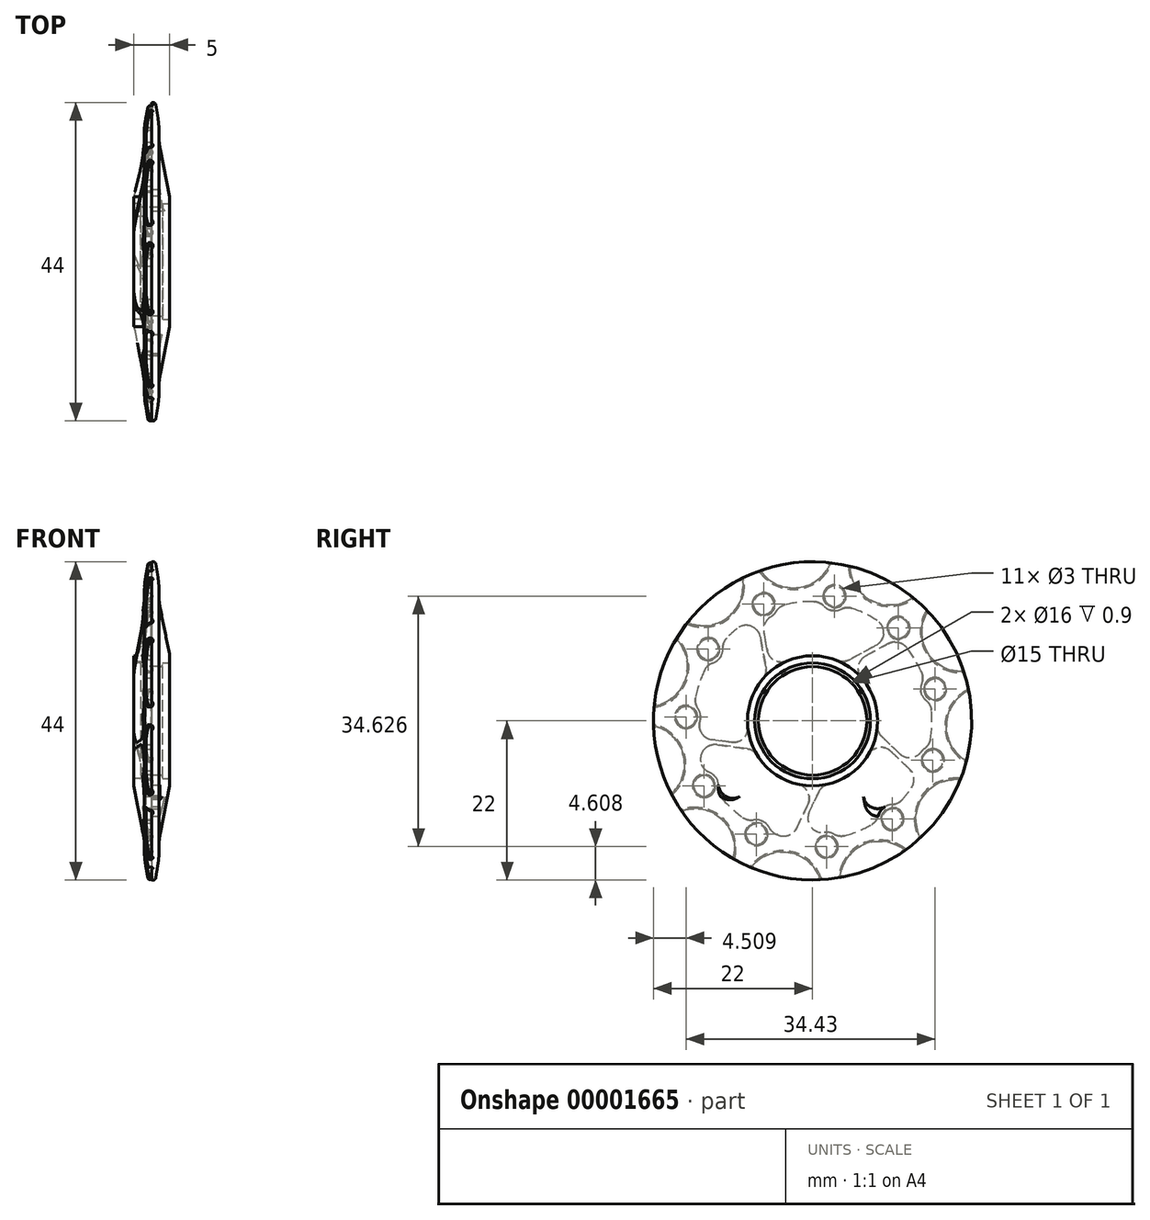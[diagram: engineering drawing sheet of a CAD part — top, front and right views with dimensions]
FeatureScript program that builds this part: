
annotation { "Feature Type Name" : "Feature", "Feature Type Description" : "" }
export const myFeature = defineFeature(function(context is Context, id is Id, definition is map)
    precondition{}
    {
        {
            var Q0;
            Q0=qCreatedBy(makeId("Front.planeOp"),FACE);
            var sketch = newSketch(context, id + "F0", { "sketchPlane" : qUnion([Q0])});
            skLineSegment(sketch, "E0.bottom", {"start": v(-2.5, 0) * mm, "end": v(2.5, 0) * mm});
            skLineSegment(sketch, "E0.top", {"start": v(-2.5, 22) * mm, "end": v(2.5, 22) * mm});
            skLineSegment(sketch, "E0.left", {"start": v(-2.5, 0) * mm, "end": v(-2.5, 22) * mm});
            skLineSegment(sketch, "E0.right", {"start": v(2.5, 0) * mm, "end": v(2.5, 22) * mm});
            skSolve(sketch);
        }
        {
            var Q0;
            Q0=makeQuery(id+"F0.imprint","IMPRINT",FACE,{"disambiguationData":[TD([[makeQuery(id+"F0.imprint","IMPRINT",EDGE,{"derivedFrom":sQuery(id+"F0.wireOp",EDGE,"E0.bottom")}),1.0]])]});
            var Q1;
            Q1=sQuery(id+"F0.wireOp",EDGE,"E0.bottom");
            revolve(context, id + "F1", {"entities" : qUnion([Q0]), "axis" : qUnion([Q1]), "revolveType" : RevolveType.FULL});
        }
        {
            var Q0;
            Q0=makeQuery(id+"F1.opRevolve","SWEPT_FACE",FACE,{"disambiguationData":[OSD([sQuery(id+"F0.wireOp",EDGE,"E0.right")])]});
            var sketch = newSketch(context, id + "F2", { "sketchPlane" : qUnion([Q0])});
            skCircle(sketch, "E1", {"center": v(0, 0) * mm, "radius": 8 * mm});
            skSolve(sketch);
        }
        {
            var Q0;
            Q0=makeQuery(id+"F2.imprint","IMPRINT",FACE,{"disambiguationData":[TD([[makeQuery(id+"F2.imprint","IMPRINT",EDGE,{"derivedFrom":sQuery(id+"F2.wireOp",EDGE,"E1")}),1.0]])]});
            extrude(context, id + "F3", {"entities" : qUnion([Q0]), "oppositeDirection" : true, "depth" : 1 * mm});
        }
        {
            var Q0;
            Q0=makeQuery(id+"F3.opExtrude","SWEPT_BODY",BODY,{"disambiguationData":[OSD([sQuery(id+"F2.wireOp",EDGE,"E1")])]});
            var Q1;
            Q1=qCreatedBy(makeId("Right.planeOp"),FACE);
            mirror(context, id + "F4", {"entities" : qUnion([Q0]), "mirrorPlane" : qUnion([Q1])});
        }
        {
            var Q0;
            Q0=makeQuery(id+"F3.opExtrude","SWEPT_BODY",BODY,{"disambiguationData":[OSD([sQuery(id+"F2.wireOp",EDGE,"E1")])]});
            var Q1;
            Q1=makeQuery(id+"F4.opPattern","COPY",BODY,{"derivedFrom":makeQuery(id+"F3.opExtrude","SWEPT_BODY",BODY,{"disambiguationData":[OSD([sQuery(id+"F2.wireOp",EDGE,"E1")])]}),"instanceName":"1"});
            var Q2;
            Q2=makeQuery(id+"F1.opRevolve","SWEPT_BODY",BODY,{"disambiguationData":[OSD([sQuery(id+"F0.wireOp",EDGE,"E0.bottom"),sQuery(id+"F0.wireOp",EDGE,"E0.top"),sQuery(id+"F0.wireOp",EDGE,"E0.left"),sQuery(id+"F0.wireOp",EDGE,"E0.right")])]});
            booleanBodies(context, id + "F5", {"operationType" : BooleanOperationType.SUBTRACTION, "tools" : qUnion([Q0, Q1]), "targets" : qUnion([Q2])});
        }
        {
            var Q0;
            Q0=makeQuery(id+"F5.opBoolean","COPY",FACE,{"derivedFrom":makeQuery(id+"F3.opExtrude","CAP_FACE",FACE,{"disambiguationData":[OSD([sQuery(id+"F2.wireOp",EDGE,"E1")])],"isStart":false})});
            var sketch = newSketch(context, id + "F6", { "sketchPlane" : qUnion([Q0])});
            skCircle(sketch, "E2", {"center": v(0, 0) * mm, "radius": 7.5 * mm});
            skSolve(sketch);
        }
        {
            var Q0;
            Q0=makeQuery(id+"F6.imprint","IMPRINT",FACE,{"disambiguationData":[TD([[makeQuery(id+"F6.imprint","IMPRINT",EDGE,{"derivedFrom":sQuery(id+"F6.wireOp",EDGE,"E2")}),1.0]])]});
            extrude(context, id + "F7", {"entities" : qUnion([Q0]), "endBound" : BoundingType.SYMMETRIC, "depth" : 50 * mm});
        }
        {
            var Q0;
            Q0=makeQuery(id+"F7.opExtrude","SWEPT_BODY",BODY,{"disambiguationData":[OSD([sQuery(id+"F6.wireOp",EDGE,"E2")])]});
            var Q1;
            Q1=makeQuery(id+"F1.opRevolve","SWEPT_BODY",BODY,{"disambiguationData":[OSD([sQuery(id+"F0.wireOp",EDGE,"E0.bottom"),sQuery(id+"F0.wireOp",EDGE,"E0.top"),sQuery(id+"F0.wireOp",EDGE,"E0.left"),sQuery(id+"F0.wireOp",EDGE,"E0.right")])]});
            booleanBodies(context, id + "F8", {"operationType" : BooleanOperationType.SUBTRACTION, "tools" : qUnion([Q0]), "targets" : qUnion([Q1])});
        }
        {
            var Q0;
            Q0=makeQuery(id+"F1.opRevolve","SWEPT_EDGE",EDGE,{"disambiguationData":[OSD([sQuery(id+"F31.wireOp",EDGE,"E87"),sQuery(id+"F31.wireOp",EDGE,"E91.5.MirrorCS")])]});
            var Q1;
            Q1=makeQuery(id+"F1.opRevolve","SWEPT_EDGE",EDGE,{"disambiguationData":[OSD([sQuery(id+"F31.wireOp",EDGE,"E91.0.MirrorCS"),sQuery(id+"F31.wireOp",EDGE,"E91.5.MirrorCS")])]});
            var Q2;
            Q2=makeQuery(id+"F5.opBoolean","COPY",EDGE,{"derivedFrom":makeQuery(id+"F4.opPattern","COPY",EDGE,{"derivedFrom":makeQuery(id+"F3.opExtrude","CAP_EDGE",EDGE,{"disambiguationData":[OSD([sQuery(id+"F2.wireOp",EDGE,"E1")])],"isStart":true}),"instanceName":"1"})});
            var Q3;
            Q3=makeQuery(id+"F8.opBoolean","INTERSECT",EDGE,{"derivedFrom":[makeQuery(id+"F5.opBoolean","COPY",FACE,{"derivedFrom":makeQuery(id+"F4.opPattern","COPY",FACE,{"derivedFrom":makeQuery(id+"F3.opExtrude","CAP_FACE",FACE,{"disambiguationData":[OSD([sQuery(id+"F2.wireOp",EDGE,"E1")])],"isStart":false}),"instanceName":"1"})}),makeQuery(id+"F7.opExtrude","SWEPT_FACE",FACE,{"disambiguationData":[OSD([sQuery(id+"F6.wireOp",EDGE,"E2")])]})]});
            var Q4;
            Q4=makeQuery(id+"F5.opBoolean","COPY",EDGE,{"derivedFrom":makeQuery(id+"F3.opExtrude","CAP_EDGE",EDGE,{"disambiguationData":[OSD([sQuery(id+"F2.wireOp",EDGE,"E1")])],"isStart":true})});
            var Q5;
            Q5=makeQuery(id+"F8.opBoolean","INTERSECT",EDGE,{"derivedFrom":[makeQuery(id+"F5.opBoolean","COPY",FACE,{"derivedFrom":makeQuery(id+"F3.opExtrude","CAP_FACE",FACE,{"disambiguationData":[OSD([sQuery(id+"F2.wireOp",EDGE,"E1")])],"isStart":false})}),makeQuery(id+"F7.opExtrude","SWEPT_FACE",FACE,{"disambiguationData":[OSD([sQuery(id+"F6.wireOp",EDGE,"E2")])]})]});
            fillet(context, id + "F9", {"entities" : qUnion([Q0, Q1, Q2, Q3, Q4, Q5]), "radius" : .3 * mm, "tangentPropagation" : true, "allowEdgeOverflow" : false});
        }
        {
            var Q0;
            Q0=makeQuery(id+"F5.opBoolean","COPY",EDGE,{"derivedFrom":makeQuery(id+"F3.opExtrude","CAP_EDGE",EDGE,{"disambiguationData":[OSD([sQuery(id+"F2.wireOp",EDGE,"E1")])],"isStart":false})});
            var Q1;
            Q1=makeQuery(id+"F5.opBoolean","COPY",EDGE,{"derivedFrom":makeQuery(id+"F4.opPattern","COPY",EDGE,{"derivedFrom":makeQuery(id+"F3.opExtrude","CAP_EDGE",EDGE,{"disambiguationData":[OSD([sQuery(id+"F2.wireOp",EDGE,"E1")])],"isStart":false}),"instanceName":"1"})});
            fillet(context, id + "F10", {"entities" : qUnion([Q0, Q1]), "radius" : .1 * mm, "tangentPropagation" : true, "allowEdgeOverflow" : false});
        }
        {
            var Q0;
            Q0=qCreatedBy(makeId("Right.planeOp"),FACE);
            var sketch = newSketch(context, id + "F11", { "sketchPlane" : qUnion([Q0])});
            skCircle(sketch, "E3", {"center": v(0, 0) * mm, "radius": 9 * mm, "construction": true});
            skCircle(sketch, "E4", {"center": v(0, 0) * mm, "radius": 16.5 * mm, "construction": true});
            skLineSegment(sketch, "E5", {"start": v(0, 0) * mm, "end": v(-7.5, 14.7) * mm, "construction": true});
            skLineSegment(sketch, "E6", {"start": v(-7.5, 14.7) * mm, "end": v(11.67, 11.67) * mm, "construction": true});
            skLineSegment(sketch, "E7", {"start": v(11.67, 11.67) * mm, "end": v(0, 0) * mm, "construction": true});
            skLineSegment(sketch, "E8", {"start": v(0, 0) * mm, "end": v(-6.02, 6.69) * mm, "construction": true});
            skLineSegment(sketch, "E9", {"start": v(-6.02, 6.69) * mm, "end": v(4.5, 7.8) * mm, "construction": true});
            skLineSegment(sketch, "E10", {"start": v(4.5, 7.8) * mm, "end": v(0, 0) * mm, "construction": true});
            skArc(sketch, "E11", {"start": v(8.9, 13.89) * mm, "mid": v(1.82, 16.4) * mm, "end": v(-5.64, 15.5) * mm});
            skArc(sketch, "E12", {"start": v(3.37, 8.35) * mm, "mid": v(-0.09, 9) * mm, "end": v(-3.53, 8.28) * mm});
            skLineSegment(sketch, "E13", {"start": v(-6.92, 13.27) * mm, "end": v(-6.28, 9.76) * mm});
            skLineSegment(sketch, "E14", {"start": v(5.07, 8.44) * mm, "end": v(8.78, 10.45) * mm});
            skLineSegment(sketch, "E15", {"start": v(4.5, 7.8) * mm, "end": v(11.67, 11.67) * mm, "construction": true});
            skLineSegment(sketch, "E16", {"start": v(-6.02, 6.69) * mm, "end": v(-7.5, 14.7) * mm, "construction": true});
            skPoint(sketch, "E17.visualSharp", {"position": v(-5.76, 6.92) * mm});
            skArc(sketch, "E17.filletArc", {"start": v(-6.28, 9.76) * mm, "mid": v(-5.26, 8.36) * mm, "end": v(-3.53, 8.28) * mm});
            skPoint(sketch, "E18.visualSharp", {"position": v(-7.21, 14.84) * mm});
            skArc(sketch, "E18.filletArc", {"start": v(-5.64, 15.5) * mm, "mid": v(-6.7, 14.62) * mm, "end": v(-6.92, 13.27) * mm});
            skPoint(sketch, "E19.visualSharp", {"position": v(11.44, 11.89) * mm});
            skArc(sketch, "E19.filletArc", {"start": v(8.78, 10.45) * mm, "mid": v(9.83, 12.13) * mm, "end": v(8.9, 13.89) * mm});
            skPoint(sketch, "E20.visualSharp", {"position": v(4.19, 7.97) * mm});
            skArc(sketch, "E20.filletArc", {"start": v(3.37, 8.35) * mm, "mid": v(4.23, 8.2) * mm, "end": v(5.07, 8.44) * mm});
            skSolve(sketch);
        }
        {
            var Q0;
            Q0=makeQuery(id+"F11.imprint","IMPRINT",FACE,{"disambiguationData":[TD([[makeQuery(id+"F11.imprint","IMPRINT",EDGE,{"derivedFrom":sQuery(id+"F11.wireOp",EDGE,"E11")}),1.0]])]});
            extrude(context, id + "F12", {"entities" : qUnion([Q0]), "depth" : 25 * mm});
        }
        {
            var Q0;
            Q0=makeQuery(id+"F12.opExtrude","SWEPT_BODY",BODY,{"disambiguationData":[OSD([sQuery(id+"F11.wireOp",EDGE,"E11"),sQuery(id+"F11.wireOp",EDGE,"E12"),sQuery(id+"F11.wireOp",EDGE,"E13"),sQuery(id+"F11.wireOp",EDGE,"E14"),sQuery(id+"F11.wireOp",EDGE,"E17.filletArc"),sQuery(id+"F11.wireOp",EDGE,"E18.filletArc"),sQuery(id+"F11.wireOp",EDGE,"E19.filletArc"),sQuery(id+"F11.wireOp",EDGE,"E20.filletArc")])]});
            var Q1;
            Q1=sQuery(id+"F0.wireOp",EDGE,"E0.bottom");
            circularPattern(context, id + "F13", {"entities" : qUnion([Q0]), "axis" : qUnion([Q1]), "angle" : 360 * degree, "instanceCount" : 10, "equalSpace" : true});
        }
        {
            var Q0;
            Q0=makeQuery(id+"F13.opPattern","COPY",BODY,{"derivedFrom":makeQuery(id+"F12.opExtrude","SWEPT_BODY",BODY,{"disambiguationData":[OSD([sQuery(id+"F11.wireOp",EDGE,"E11"),sQuery(id+"F11.wireOp",EDGE,"E12"),sQuery(id+"F11.wireOp",EDGE,"E13"),sQuery(id+"F11.wireOp",EDGE,"E14"),sQuery(id+"F11.wireOp",EDGE,"E17.filletArc"),sQuery(id+"F11.wireOp",EDGE,"E18.filletArc"),sQuery(id+"F11.wireOp",EDGE,"E19.filletArc"),sQuery(id+"F11.wireOp",EDGE,"E20.filletArc")])]}),"instanceName":"1"});
            var Q1;
            Q1=makeQuery(id+"F13.opPattern","COPY",BODY,{"derivedFrom":makeQuery(id+"F12.opExtrude","SWEPT_BODY",BODY,{"disambiguationData":[OSD([sQuery(id+"F11.wireOp",EDGE,"E11"),sQuery(id+"F11.wireOp",EDGE,"E12"),sQuery(id+"F11.wireOp",EDGE,"E13"),sQuery(id+"F11.wireOp",EDGE,"E14"),sQuery(id+"F11.wireOp",EDGE,"E17.filletArc"),sQuery(id+"F11.wireOp",EDGE,"E18.filletArc"),sQuery(id+"F11.wireOp",EDGE,"E19.filletArc"),sQuery(id+"F11.wireOp",EDGE,"E20.filletArc")])]}),"instanceName":"9"});
            var Q2;
            Q2=makeQuery(id+"F13.opPattern","COPY",BODY,{"derivedFrom":makeQuery(id+"F12.opExtrude","SWEPT_BODY",BODY,{"disambiguationData":[OSD([sQuery(id+"F11.wireOp",EDGE,"E11"),sQuery(id+"F11.wireOp",EDGE,"E12"),sQuery(id+"F11.wireOp",EDGE,"E13"),sQuery(id+"F11.wireOp",EDGE,"E14"),sQuery(id+"F11.wireOp",EDGE,"E17.filletArc"),sQuery(id+"F11.wireOp",EDGE,"E18.filletArc"),sQuery(id+"F11.wireOp",EDGE,"E19.filletArc"),sQuery(id+"F11.wireOp",EDGE,"E20.filletArc")])]}),"instanceName":"7"});
            var Q3;
            Q3=makeQuery(id+"F13.opPattern","COPY",BODY,{"derivedFrom":makeQuery(id+"F12.opExtrude","SWEPT_BODY",BODY,{"disambiguationData":[OSD([sQuery(id+"F11.wireOp",EDGE,"E11"),sQuery(id+"F11.wireOp",EDGE,"E12"),sQuery(id+"F11.wireOp",EDGE,"E13"),sQuery(id+"F11.wireOp",EDGE,"E14"),sQuery(id+"F11.wireOp",EDGE,"E17.filletArc"),sQuery(id+"F11.wireOp",EDGE,"E18.filletArc"),sQuery(id+"F11.wireOp",EDGE,"E19.filletArc"),sQuery(id+"F11.wireOp",EDGE,"E20.filletArc")])]}),"instanceName":"3"});
            var Q4;
            Q4=makeQuery(id+"F13.opPattern","COPY",BODY,{"derivedFrom":makeQuery(id+"F12.opExtrude","SWEPT_BODY",BODY,{"disambiguationData":[OSD([sQuery(id+"F11.wireOp",EDGE,"E11"),sQuery(id+"F11.wireOp",EDGE,"E12"),sQuery(id+"F11.wireOp",EDGE,"E13"),sQuery(id+"F11.wireOp",EDGE,"E14"),sQuery(id+"F11.wireOp",EDGE,"E17.filletArc"),sQuery(id+"F11.wireOp",EDGE,"E18.filletArc"),sQuery(id+"F11.wireOp",EDGE,"E19.filletArc"),sQuery(id+"F11.wireOp",EDGE,"E20.filletArc")])]}),"instanceName":"5"});
            var Q5;
            Q5=makeQuery(id+"F1.opRevolve","SWEPT_BODY",BODY,{"disambiguationData":[OSD([sQuery(id+"F0.wireOp",EDGE,"E0.bottom"),sQuery(id+"F0.wireOp",EDGE,"E0.top"),sQuery(id+"F0.wireOp",EDGE,"E0.left"),sQuery(id+"F0.wireOp",EDGE,"E0.right")])]});
            booleanBodies(context, id + "F14", {"operationType" : BooleanOperationType.SUBTRACTION, "tools" : qUnion([Q0, Q1, Q2, Q3, Q4]), "targets" : qUnion([Q5])});
        }
        {
            var Q0;
            Q0=makeQuery(id+"F12.opExtrude","SWEPT_BODY",BODY,{"disambiguationData":[OSD([sQuery(id+"F11.wireOp",EDGE,"E11"),sQuery(id+"F11.wireOp",EDGE,"E12"),sQuery(id+"F11.wireOp",EDGE,"E13"),sQuery(id+"F11.wireOp",EDGE,"E14"),sQuery(id+"F11.wireOp",EDGE,"E17.filletArc"),sQuery(id+"F11.wireOp",EDGE,"E18.filletArc"),sQuery(id+"F11.wireOp",EDGE,"E19.filletArc"),sQuery(id+"F11.wireOp",EDGE,"E20.filletArc")])]});
            var Q1;
            Q1=makeQuery(id+"F13.opPattern","COPY",BODY,{"derivedFrom":makeQuery(id+"F12.opExtrude","SWEPT_BODY",BODY,{"disambiguationData":[OSD([sQuery(id+"F11.wireOp",EDGE,"E11"),sQuery(id+"F11.wireOp",EDGE,"E12"),sQuery(id+"F11.wireOp",EDGE,"E13"),sQuery(id+"F11.wireOp",EDGE,"E14"),sQuery(id+"F11.wireOp",EDGE,"E17.filletArc"),sQuery(id+"F11.wireOp",EDGE,"E18.filletArc"),sQuery(id+"F11.wireOp",EDGE,"E19.filletArc"),sQuery(id+"F11.wireOp",EDGE,"E20.filletArc")])]}),"instanceName":"2"});
            var Q2;
            Q2=makeQuery(id+"F13.opPattern","COPY",BODY,{"derivedFrom":makeQuery(id+"F12.opExtrude","SWEPT_BODY",BODY,{"disambiguationData":[OSD([sQuery(id+"F11.wireOp",EDGE,"E11"),sQuery(id+"F11.wireOp",EDGE,"E12"),sQuery(id+"F11.wireOp",EDGE,"E13"),sQuery(id+"F11.wireOp",EDGE,"E14"),sQuery(id+"F11.wireOp",EDGE,"E17.filletArc"),sQuery(id+"F11.wireOp",EDGE,"E18.filletArc"),sQuery(id+"F11.wireOp",EDGE,"E19.filletArc"),sQuery(id+"F11.wireOp",EDGE,"E20.filletArc")])]}),"instanceName":"4"});
            var Q3;
            Q3=makeQuery(id+"F13.opPattern","COPY",BODY,{"derivedFrom":makeQuery(id+"F12.opExtrude","SWEPT_BODY",BODY,{"disambiguationData":[OSD([sQuery(id+"F11.wireOp",EDGE,"E11"),sQuery(id+"F11.wireOp",EDGE,"E12"),sQuery(id+"F11.wireOp",EDGE,"E13"),sQuery(id+"F11.wireOp",EDGE,"E14"),sQuery(id+"F11.wireOp",EDGE,"E17.filletArc"),sQuery(id+"F11.wireOp",EDGE,"E18.filletArc"),sQuery(id+"F11.wireOp",EDGE,"E19.filletArc"),sQuery(id+"F11.wireOp",EDGE,"E20.filletArc")])]}),"instanceName":"6"});
            var Q4;
            Q4=makeQuery(id+"F13.opPattern","COPY",BODY,{"derivedFrom":makeQuery(id+"F12.opExtrude","SWEPT_BODY",BODY,{"disambiguationData":[OSD([sQuery(id+"F11.wireOp",EDGE,"E11"),sQuery(id+"F11.wireOp",EDGE,"E12"),sQuery(id+"F11.wireOp",EDGE,"E13"),sQuery(id+"F11.wireOp",EDGE,"E14"),sQuery(id+"F11.wireOp",EDGE,"E17.filletArc"),sQuery(id+"F11.wireOp",EDGE,"E18.filletArc"),sQuery(id+"F11.wireOp",EDGE,"E19.filletArc"),sQuery(id+"F11.wireOp",EDGE,"E20.filletArc")])]}),"instanceName":"8"});
            var Q5;
            Q5=qCreatedBy(makeId("Right.planeOp"),FACE);
            mirror(context, id + "F15", {"entities" : qUnion([Q0, Q1, Q2, Q3, Q4]), "mirrorPlane" : qUnion([Q5])});
        }
        {
            var Q0;
            Q0=makeQuery(id+"F15.opPattern","COPY",BODY,{"derivedFrom":makeQuery(id+"F13.opPattern","COPY",BODY,{"derivedFrom":makeQuery(id+"F12.opExtrude","SWEPT_BODY",BODY,{"disambiguationData":[OSD([sQuery(id+"F11.wireOp",EDGE,"E11"),sQuery(id+"F11.wireOp",EDGE,"E12"),sQuery(id+"F11.wireOp",EDGE,"E13"),sQuery(id+"F11.wireOp",EDGE,"E14"),sQuery(id+"F11.wireOp",EDGE,"E17.filletArc"),sQuery(id+"F11.wireOp",EDGE,"E18.filletArc"),sQuery(id+"F11.wireOp",EDGE,"E19.filletArc"),sQuery(id+"F11.wireOp",EDGE,"E20.filletArc")])]}),"instanceName":"2"}),"instanceName":"1"});
            var Q1;
            Q1=makeQuery(id+"F15.opPattern","COPY",BODY,{"derivedFrom":makeQuery(id+"F12.opExtrude","SWEPT_BODY",BODY,{"disambiguationData":[OSD([sQuery(id+"F11.wireOp",EDGE,"E11"),sQuery(id+"F11.wireOp",EDGE,"E12"),sQuery(id+"F11.wireOp",EDGE,"E13"),sQuery(id+"F11.wireOp",EDGE,"E14"),sQuery(id+"F11.wireOp",EDGE,"E17.filletArc"),sQuery(id+"F11.wireOp",EDGE,"E18.filletArc"),sQuery(id+"F11.wireOp",EDGE,"E19.filletArc"),sQuery(id+"F11.wireOp",EDGE,"E20.filletArc")])]}),"instanceName":"1"});
            var Q2;
            Q2=makeQuery(id+"F15.opPattern","COPY",BODY,{"derivedFrom":makeQuery(id+"F13.opPattern","COPY",BODY,{"derivedFrom":makeQuery(id+"F12.opExtrude","SWEPT_BODY",BODY,{"disambiguationData":[OSD([sQuery(id+"F11.wireOp",EDGE,"E11"),sQuery(id+"F11.wireOp",EDGE,"E12"),sQuery(id+"F11.wireOp",EDGE,"E13"),sQuery(id+"F11.wireOp",EDGE,"E14"),sQuery(id+"F11.wireOp",EDGE,"E17.filletArc"),sQuery(id+"F11.wireOp",EDGE,"E18.filletArc"),sQuery(id+"F11.wireOp",EDGE,"E19.filletArc"),sQuery(id+"F11.wireOp",EDGE,"E20.filletArc")])]}),"instanceName":"4"}),"instanceName":"1"});
            var Q3;
            Q3=makeQuery(id+"F15.opPattern","COPY",BODY,{"derivedFrom":makeQuery(id+"F13.opPattern","COPY",BODY,{"derivedFrom":makeQuery(id+"F12.opExtrude","SWEPT_BODY",BODY,{"disambiguationData":[OSD([sQuery(id+"F11.wireOp",EDGE,"E11"),sQuery(id+"F11.wireOp",EDGE,"E12"),sQuery(id+"F11.wireOp",EDGE,"E13"),sQuery(id+"F11.wireOp",EDGE,"E14"),sQuery(id+"F11.wireOp",EDGE,"E17.filletArc"),sQuery(id+"F11.wireOp",EDGE,"E18.filletArc"),sQuery(id+"F11.wireOp",EDGE,"E19.filletArc"),sQuery(id+"F11.wireOp",EDGE,"E20.filletArc")])]}),"instanceName":"6"}),"instanceName":"1"});
            var Q4;
            Q4=makeQuery(id+"F15.opPattern","COPY",BODY,{"derivedFrom":makeQuery(id+"F13.opPattern","COPY",BODY,{"derivedFrom":makeQuery(id+"F12.opExtrude","SWEPT_BODY",BODY,{"disambiguationData":[OSD([sQuery(id+"F11.wireOp",EDGE,"E11"),sQuery(id+"F11.wireOp",EDGE,"E12"),sQuery(id+"F11.wireOp",EDGE,"E13"),sQuery(id+"F11.wireOp",EDGE,"E14"),sQuery(id+"F11.wireOp",EDGE,"E17.filletArc"),sQuery(id+"F11.wireOp",EDGE,"E18.filletArc"),sQuery(id+"F11.wireOp",EDGE,"E19.filletArc"),sQuery(id+"F11.wireOp",EDGE,"E20.filletArc")])]}),"instanceName":"8"}),"instanceName":"1"});
            var Q5;
            Q5=makeQuery(id+"F1.opRevolve","SWEPT_BODY",BODY,{"disambiguationData":[OSD([sQuery(id+"F0.wireOp",EDGE,"E0.bottom"),sQuery(id+"F0.wireOp",EDGE,"E0.top"),sQuery(id+"F0.wireOp",EDGE,"E0.left"),sQuery(id+"F0.wireOp",EDGE,"E0.right")])]});
            booleanBodies(context, id + "F16", {"operationType" : BooleanOperationType.SUBTRACTION, "tools" : qUnion([Q0, Q1, Q2, Q3, Q4]), "targets" : qUnion([Q5])});
        }
        {
            var Q0;
            Q0=makeQuery(id+"F13.opPattern","COPY",BODY,{"derivedFrom":makeQuery(id+"F12.opExtrude","SWEPT_BODY",BODY,{"disambiguationData":[OSD([sQuery(id+"F11.wireOp",EDGE,"E11"),sQuery(id+"F11.wireOp",EDGE,"E12"),sQuery(id+"F11.wireOp",EDGE,"E13"),sQuery(id+"F11.wireOp",EDGE,"E14"),sQuery(id+"F11.wireOp",EDGE,"E17.filletArc"),sQuery(id+"F11.wireOp",EDGE,"E18.filletArc"),sQuery(id+"F11.wireOp",EDGE,"E19.filletArc"),sQuery(id+"F11.wireOp",EDGE,"E20.filletArc")])]}),"instanceName":"2"});
            var Q1;
            Q1=makeQuery(id+"F12.opExtrude","SWEPT_BODY",BODY,{"disambiguationData":[OSD([sQuery(id+"F11.wireOp",EDGE,"E11"),sQuery(id+"F11.wireOp",EDGE,"E12"),sQuery(id+"F11.wireOp",EDGE,"E13"),sQuery(id+"F11.wireOp",EDGE,"E14"),sQuery(id+"F11.wireOp",EDGE,"E17.filletArc"),sQuery(id+"F11.wireOp",EDGE,"E18.filletArc"),sQuery(id+"F11.wireOp",EDGE,"E19.filletArc"),sQuery(id+"F11.wireOp",EDGE,"E20.filletArc")])]});
            var Q2;
            Q2=makeQuery(id+"F13.opPattern","COPY",BODY,{"derivedFrom":makeQuery(id+"F12.opExtrude","SWEPT_BODY",BODY,{"disambiguationData":[OSD([sQuery(id+"F11.wireOp",EDGE,"E11"),sQuery(id+"F11.wireOp",EDGE,"E12"),sQuery(id+"F11.wireOp",EDGE,"E13"),sQuery(id+"F11.wireOp",EDGE,"E14"),sQuery(id+"F11.wireOp",EDGE,"E17.filletArc"),sQuery(id+"F11.wireOp",EDGE,"E18.filletArc"),sQuery(id+"F11.wireOp",EDGE,"E19.filletArc"),sQuery(id+"F11.wireOp",EDGE,"E20.filletArc")])]}),"instanceName":"8"});
            var Q3;
            Q3=makeQuery(id+"F13.opPattern","COPY",BODY,{"derivedFrom":makeQuery(id+"F12.opExtrude","SWEPT_BODY",BODY,{"disambiguationData":[OSD([sQuery(id+"F11.wireOp",EDGE,"E11"),sQuery(id+"F11.wireOp",EDGE,"E12"),sQuery(id+"F11.wireOp",EDGE,"E13"),sQuery(id+"F11.wireOp",EDGE,"E14"),sQuery(id+"F11.wireOp",EDGE,"E17.filletArc"),sQuery(id+"F11.wireOp",EDGE,"E18.filletArc"),sQuery(id+"F11.wireOp",EDGE,"E19.filletArc"),sQuery(id+"F11.wireOp",EDGE,"E20.filletArc")])]}),"instanceName":"6"});
            var Q4;
            Q4=makeQuery(id+"F13.opPattern","COPY",BODY,{"derivedFrom":makeQuery(id+"F12.opExtrude","SWEPT_BODY",BODY,{"disambiguationData":[OSD([sQuery(id+"F11.wireOp",EDGE,"E11"),sQuery(id+"F11.wireOp",EDGE,"E12"),sQuery(id+"F11.wireOp",EDGE,"E13"),sQuery(id+"F11.wireOp",EDGE,"E14"),sQuery(id+"F11.wireOp",EDGE,"E17.filletArc"),sQuery(id+"F11.wireOp",EDGE,"E18.filletArc"),sQuery(id+"F11.wireOp",EDGE,"E19.filletArc"),sQuery(id+"F11.wireOp",EDGE,"E20.filletArc")])]}),"instanceName":"4"});
            deleteBodies(context, id + "F17", {"entities" : qUnion([Q0, Q1, Q2, Q3, Q4])});
        }
        {
            var Q0;
            Q0=qCreatedBy(makeId("Right.planeOp"),FACE);
            var sketch = newSketch(context, id + "F18", { "sketchPlane" : qUnion([Q0])});
            skCircle(sketch, "E21", {"center": v(10.66, 21.5) * mm, "radius": 5.5 * mm});
            skLineSegment(sketch, "E22", {"start": v(0, 0) * mm, "end": v(10.66, 21.5) * mm, "construction": true});
            skLineSegment(sketch, "E23", {"start": v(-2.66, 23.85) * mm, "end": v(0, 0) * mm, "construction": true});
            skLineSegment(sketch, "E24", {"start": v(-2.66, 23.85) * mm, "end": v(10.66, 21.5) * mm, "construction": true});
            skCircle(sketch, "E25", {"center": v(-2.66, 23.85) * mm, "radius": 5.5 * mm, "construction": true});
            skLineSegment(sketch, "E26", {"start": v(4, 22.68) * mm, "end": v(3.04, 17.23) * mm, "construction": true});
            skCircle(sketch, "E27", {"center": v(3.04, 17.23) * mm, "radius": 1.5 * mm});
            skArc(sketch, "E28", {"start": v(1.07, 17.58) * mm, "mid": v(2.7, 15.26) * mm, "end": v(5, 16.89) * mm});
            skLineSegment(sketch, "E29", {"start": v(1.07, 17.58) * mm, "end": v(1.56, 17.5) * mm});
            skLineSegment(sketch, "E30.trimOffspring", {"start": v(4.52, 16.97) * mm, "end": v(5, 16.89) * mm});
            skLineSegment(sketch, "E31", {"start": v(3.04, 17.23) * mm, "end": v(0, 0) * mm, "construction": true});
            skSolve(sketch);
        }
        {
            var Q0;
            Q0=makeQuery(id+"F18.imprint","IMPRINT",FACE,{"disambiguationData":[TD([[makeQuery(id+"F18.imprint","IMPRINT",EDGE,{"derivedFrom":sQuery(id+"F18.wireOp",EDGE,"E28")}),1.0]])]});
            var Q1;
            Q1=makeQuery(id+"F1.opRevolve","SWEPT_FACE",FACE,{"disambiguationData":[OSD([sQuery(id+"F0.wireOp",EDGE,"E0.right")])]});
            extrude(context, id + "F19", {"entities" : qUnion([Q0]), "endBound" : BoundingType.UP_TO_SURFACE, "endBoundEntityFace" : qUnion([Q1]), "depth" : 2 * mm});
        }
        {
            var Q0;
            Q0=makeQuery(id+"F19.opExtrude","CAP_FACE",FACE,{"disambiguationData":[OSD([sQuery(id+"F18.wireOp",EDGE,"E27"),sQuery(id+"F18.wireOp",EDGE,"E28"),sQuery(id+"F18.wireOp",EDGE,"E29"),sQuery(id+"F18.wireOp",EDGE,"E30.trimOffspring")])],"isStart":true});
            var Q1;
            Q1=makeQuery(id+"F1.opRevolve","SWEPT_FACE",FACE,{"disambiguationData":[OSD([sQuery(id+"F0.wireOp",EDGE,"E0.left")])]});
            extrude(context, id + "F20", {"entities" : qUnion([Q0]), "endBound" : BoundingType.UP_TO_SURFACE, "endBoundEntityFace" : qUnion([Q1]), "depth" : 25 * mm});
        }
        {
            var Q0;
            Q0=makeQuery(id+"F19.opExtrude","SWEPT_BODY",BODY,{"disambiguationData":[OSD([sQuery(id+"F18.wireOp",EDGE,"E27"),sQuery(id+"F18.wireOp",EDGE,"E28"),sQuery(id+"F18.wireOp",EDGE,"E29"),sQuery(id+"F18.wireOp",EDGE,"E30.trimOffspring")])]});
            var Q1;
            Q1=makeQuery(id+"F20.opExtrude","SWEPT_BODY",BODY,{"disambiguationData":[OSD([sQuery(id+"F18.wireOp",EDGE,"E27"),sQuery(id+"F18.wireOp",EDGE,"E28"),sQuery(id+"F18.wireOp",EDGE,"E29"),sQuery(id+"F18.wireOp",EDGE,"E30.trimOffspring")])]});
            booleanBodies(context, id + "F21", {"operationType" : BooleanOperationType.UNION, "tools" : qUnion([Q0, Q1])});
        }
        {
            var Q0;
            Q0=makeQuery(id+"F18.imprint","IMPRINT",FACE,{"disambiguationData":[TD([[makeQuery(id+"F18.imprint","IMPRINT",EDGE,{"derivedFrom":sQuery(id+"F18.wireOp",EDGE,"E21")}),1.0]])]});
            var Q1;
            {var subQ0=sQuery(id+"F18.wireOp",EDGE,"E27");var subQ2=makeQuery(id+"F18.imprint","INTERSECT",VERTEX,{"derivedFrom":[subQ0,sQuery(id+"F18.wireOp",EDGE,"E29")]});Q1=makeQuery(id+"F18.imprint","IMPRINT",FACE,{"disambiguationData":[TD([[makeQuery(id+"F18.imprint","IMPRINT",EDGE,{"disambiguationData":[TD([[subQ2,-1.0]])],"derivedFrom":subQ0}),1.0]])]});}
            extrude(context, id + "F22", {"entities" : qUnion([Q0, Q1]), "endBound" : BoundingType.SYMMETRIC, "depth" : 50 * mm});
        }
        {
            var Q0;
            Q0=makeQuery(id+"F22.opExtrude","SWEPT_BODY",BODY,{"disambiguationData":[OSD([sQuery(id+"F18.wireOp",EDGE,"E21")])]});
            var Q1;
            Q1=makeQuery(id+"F22.opExtrude","SWEPT_BODY",BODY,{"disambiguationData":[OSD([sQuery(id+"F18.wireOp",EDGE,"E27")])]});
            var Q2;
            Q2=makeQuery(id+"F19.opExtrude","SWEPT_BODY",BODY,{"disambiguationData":[OSD([sQuery(id+"F18.wireOp",EDGE,"E27"),sQuery(id+"F18.wireOp",EDGE,"E28"),sQuery(id+"F18.wireOp",EDGE,"E29"),sQuery(id+"F18.wireOp",EDGE,"E30.trimOffspring")])]});
            var Q3;
            Q3=sQuery(id+"F0.wireOp",EDGE,"E0.bottom");
            circularPattern(context, id + "F23", {"entities" : qUnion([Q0, Q1, Q2]), "axis" : qUnion([Q3]), "angle" : 360 * degree, "instanceCount" : 11, "equalSpace" : true});
        }
        {
            var Q0;
            Q0=makeQuery(id+"F23.opPattern","COPY",BODY,{"derivedFrom":makeQuery(id+"F22.opExtrude","SWEPT_BODY",BODY,{"disambiguationData":[OSD([sQuery(id+"F18.wireOp",EDGE,"E21")])]}),"instanceName":"1"});
            var Q1;
            Q1=makeQuery(id+"F22.opExtrude","SWEPT_BODY",BODY,{"disambiguationData":[OSD([sQuery(id+"F18.wireOp",EDGE,"E21")])]});
            var Q2;
            Q2=makeQuery(id+"F22.opExtrude","SWEPT_BODY",BODY,{"disambiguationData":[OSD([sQuery(id+"F18.wireOp",EDGE,"E27")])]});
            var Q3;
            Q3=makeQuery(id+"F23.opPattern","COPY",BODY,{"derivedFrom":makeQuery(id+"F22.opExtrude","SWEPT_BODY",BODY,{"disambiguationData":[OSD([sQuery(id+"F18.wireOp",EDGE,"E27")])]}),"instanceName":"4"});
            var Q4;
            Q4=makeQuery(id+"F23.opPattern","COPY",BODY,{"derivedFrom":makeQuery(id+"F22.opExtrude","SWEPT_BODY",BODY,{"disambiguationData":[OSD([sQuery(id+"F18.wireOp",EDGE,"E27")])]}),"instanceName":"3"});
            var Q5;
            Q5=makeQuery(id+"F23.opPattern","COPY",BODY,{"derivedFrom":makeQuery(id+"F22.opExtrude","SWEPT_BODY",BODY,{"disambiguationData":[OSD([sQuery(id+"F18.wireOp",EDGE,"E21")])]}),"instanceName":"3"});
            var Q6;
            Q6=makeQuery(id+"F23.opPattern","COPY",BODY,{"derivedFrom":makeQuery(id+"F22.opExtrude","SWEPT_BODY",BODY,{"disambiguationData":[OSD([sQuery(id+"F18.wireOp",EDGE,"E21")])]}),"instanceName":"5"});
            var Q7;
            Q7=makeQuery(id+"F23.opPattern","COPY",BODY,{"derivedFrom":makeQuery(id+"F22.opExtrude","SWEPT_BODY",BODY,{"disambiguationData":[OSD([sQuery(id+"F18.wireOp",EDGE,"E21")])]}),"instanceName":"2"});
            var Q8;
            Q8=makeQuery(id+"F23.opPattern","COPY",BODY,{"derivedFrom":makeQuery(id+"F22.opExtrude","SWEPT_BODY",BODY,{"disambiguationData":[OSD([sQuery(id+"F18.wireOp",EDGE,"E27")])]}),"instanceName":"5"});
            var Q9;
            Q9=makeQuery(id+"F23.opPattern","COPY",BODY,{"derivedFrom":makeQuery(id+"F22.opExtrude","SWEPT_BODY",BODY,{"disambiguationData":[OSD([sQuery(id+"F18.wireOp",EDGE,"E27")])]}),"instanceName":"1"});
            var Q10;
            Q10=makeQuery(id+"F23.opPattern","COPY",BODY,{"derivedFrom":makeQuery(id+"F22.opExtrude","SWEPT_BODY",BODY,{"disambiguationData":[OSD([sQuery(id+"F18.wireOp",EDGE,"E21")])]}),"instanceName":"4"});
            var Q11;
            Q11=makeQuery(id+"F23.opPattern","COPY",BODY,{"derivedFrom":makeQuery(id+"F22.opExtrude","SWEPT_BODY",BODY,{"disambiguationData":[OSD([sQuery(id+"F18.wireOp",EDGE,"E27")])]}),"instanceName":"9"});
            var Q12;
            Q12=makeQuery(id+"F23.opPattern","COPY",BODY,{"derivedFrom":makeQuery(id+"F22.opExtrude","SWEPT_BODY",BODY,{"disambiguationData":[OSD([sQuery(id+"F18.wireOp",EDGE,"E27")])]}),"instanceName":"6"});
            var Q13;
            Q13=makeQuery(id+"F23.opPattern","COPY",BODY,{"derivedFrom":makeQuery(id+"F22.opExtrude","SWEPT_BODY",BODY,{"disambiguationData":[OSD([sQuery(id+"F18.wireOp",EDGE,"E21")])]}),"instanceName":"10"});
            var Q14;
            Q14=makeQuery(id+"F23.opPattern","COPY",BODY,{"derivedFrom":makeQuery(id+"F22.opExtrude","SWEPT_BODY",BODY,{"disambiguationData":[OSD([sQuery(id+"F18.wireOp",EDGE,"E21")])]}),"instanceName":"7"});
            var Q15;
            Q15=makeQuery(id+"F23.opPattern","COPY",BODY,{"derivedFrom":makeQuery(id+"F22.opExtrude","SWEPT_BODY",BODY,{"disambiguationData":[OSD([sQuery(id+"F18.wireOp",EDGE,"E27")])]}),"instanceName":"2"});
            var Q16;
            Q16=makeQuery(id+"F23.opPattern","COPY",BODY,{"derivedFrom":makeQuery(id+"F22.opExtrude","SWEPT_BODY",BODY,{"disambiguationData":[OSD([sQuery(id+"F18.wireOp",EDGE,"E21")])]}),"instanceName":"9"});
            var Q17;
            Q17=makeQuery(id+"F23.opPattern","COPY",BODY,{"derivedFrom":makeQuery(id+"F22.opExtrude","SWEPT_BODY",BODY,{"disambiguationData":[OSD([sQuery(id+"F18.wireOp",EDGE,"E27")])]}),"instanceName":"10"});
            var Q18;
            Q18=makeQuery(id+"F23.opPattern","COPY",BODY,{"derivedFrom":makeQuery(id+"F22.opExtrude","SWEPT_BODY",BODY,{"disambiguationData":[OSD([sQuery(id+"F18.wireOp",EDGE,"E27")])]}),"instanceName":"7"});
            var Q19;
            Q19=makeQuery(id+"F23.opPattern","COPY",BODY,{"derivedFrom":makeQuery(id+"F22.opExtrude","SWEPT_BODY",BODY,{"disambiguationData":[OSD([sQuery(id+"F18.wireOp",EDGE,"E21")])]}),"instanceName":"6"});
            var Q20;
            Q20=makeQuery(id+"F23.opPattern","COPY",BODY,{"derivedFrom":makeQuery(id+"F22.opExtrude","SWEPT_BODY",BODY,{"disambiguationData":[OSD([sQuery(id+"F18.wireOp",EDGE,"E21")])]}),"instanceName":"8"});
            var Q21;
            Q21=makeQuery(id+"F23.opPattern","COPY",BODY,{"derivedFrom":makeQuery(id+"F22.opExtrude","SWEPT_BODY",BODY,{"disambiguationData":[OSD([sQuery(id+"F18.wireOp",EDGE,"E27")])]}),"instanceName":"8"});
            var Q22;
            Q22=makeQuery(id+"F1.opRevolve","SWEPT_BODY",BODY,{"disambiguationData":[OSD([sQuery(id+"F31.wireOp",EDGE,"E85"),sQuery(id+"F31.wireOp",EDGE,"E86"),sQuery(id+"F31.wireOp",EDGE,"E87"),sQuery(id+"F31.wireOp",EDGE,"E89"),sQuery(id+"F31.wireOp",EDGE,"E90"),sQuery(id+"F31.wireOp",EDGE,"E91.0.MirrorCS"),sQuery(id+"F31.wireOp",EDGE,"E91.2.MirrorCS"),sQuery(id+"F31.wireOp",EDGE,"E91.3.MirrorCS"),sQuery(id+"F31.wireOp",EDGE,"E91.4.MirrorCS"),sQuery(id+"F31.wireOp",EDGE,"E91.5.MirrorCS")])]});
            var Q23;
            Q23=makeQuery(id+"F1.opRevolve","SWEPT_BODY",BODY,{"disambiguationData":[OSD([sQuery(id+"F0.wireOp",EDGE,"E0.bottom"),sQuery(id+"F0.wireOp",EDGE,"E0.top"),sQuery(id+"F0.wireOp",EDGE,"E0.left"),sQuery(id+"F0.wireOp",EDGE,"E0.right")])]});
            booleanBodies(context, id + "F24", {"operationType" : BooleanOperationType.SUBTRACTION, "tools" : qUnion([Q0, Q1, Q2, Q3, Q4, Q5, Q6, Q7, Q8, Q9, Q10, Q11, Q12, Q13, Q14, Q15, Q16, Q17, Q18, Q19, Q20, Q21]), "targets" : qUnion([Q22, Q23])});
        }
        {
            var Q0;
            Q0=makeQuery(id+"F23.opPattern","COPY",BODY,{"derivedFrom":makeQuery(id+"F19.opExtrude","SWEPT_BODY",BODY,{"disambiguationData":[OSD([sQuery(id+"F18.wireOp",EDGE,"E27"),sQuery(id+"F18.wireOp",EDGE,"E28"),sQuery(id+"F18.wireOp",EDGE,"E29"),sQuery(id+"F18.wireOp",EDGE,"E30.trimOffspring")])]}),"instanceName":"1"});
            var Q1;
            Q1=makeQuery(id+"F23.opPattern","COPY",BODY,{"derivedFrom":makeQuery(id+"F19.opExtrude","SWEPT_BODY",BODY,{"disambiguationData":[OSD([sQuery(id+"F18.wireOp",EDGE,"E27"),sQuery(id+"F18.wireOp",EDGE,"E28"),sQuery(id+"F18.wireOp",EDGE,"E29"),sQuery(id+"F18.wireOp",EDGE,"E30.trimOffspring")])]}),"instanceName":"10"});
            var Q2;
            Q2=makeQuery(id+"F23.opPattern","COPY",BODY,{"derivedFrom":makeQuery(id+"F19.opExtrude","SWEPT_BODY",BODY,{"disambiguationData":[OSD([sQuery(id+"F18.wireOp",EDGE,"E27"),sQuery(id+"F18.wireOp",EDGE,"E28"),sQuery(id+"F18.wireOp",EDGE,"E29"),sQuery(id+"F18.wireOp",EDGE,"E30.trimOffspring")])]}),"instanceName":"3"});
            var Q3;
            Q3=makeQuery(id+"F23.opPattern","COPY",BODY,{"derivedFrom":makeQuery(id+"F19.opExtrude","SWEPT_BODY",BODY,{"disambiguationData":[OSD([sQuery(id+"F18.wireOp",EDGE,"E27"),sQuery(id+"F18.wireOp",EDGE,"E28"),sQuery(id+"F18.wireOp",EDGE,"E29"),sQuery(id+"F18.wireOp",EDGE,"E30.trimOffspring")])]}),"instanceName":"5"});
            var Q4;
            Q4=makeQuery(id+"F23.opPattern","COPY",BODY,{"derivedFrom":makeQuery(id+"F19.opExtrude","SWEPT_BODY",BODY,{"disambiguationData":[OSD([sQuery(id+"F18.wireOp",EDGE,"E27"),sQuery(id+"F18.wireOp",EDGE,"E28"),sQuery(id+"F18.wireOp",EDGE,"E29"),sQuery(id+"F18.wireOp",EDGE,"E30.trimOffspring")])]}),"instanceName":"6"});
            var Q5;
            Q5=makeQuery(id+"F23.opPattern","COPY",BODY,{"derivedFrom":makeQuery(id+"F19.opExtrude","SWEPT_BODY",BODY,{"disambiguationData":[OSD([sQuery(id+"F18.wireOp",EDGE,"E27"),sQuery(id+"F18.wireOp",EDGE,"E28"),sQuery(id+"F18.wireOp",EDGE,"E29"),sQuery(id+"F18.wireOp",EDGE,"E30.trimOffspring")])]}),"instanceName":"4"});
            var Q6;
            Q6=makeQuery(id+"F23.opPattern","COPY",BODY,{"derivedFrom":makeQuery(id+"F19.opExtrude","SWEPT_BODY",BODY,{"disambiguationData":[OSD([sQuery(id+"F18.wireOp",EDGE,"E27"),sQuery(id+"F18.wireOp",EDGE,"E28"),sQuery(id+"F18.wireOp",EDGE,"E29"),sQuery(id+"F18.wireOp",EDGE,"E30.trimOffspring")])]}),"instanceName":"7"});
            var Q7;
            Q7=makeQuery(id+"F19.opExtrude","SWEPT_BODY",BODY,{"disambiguationData":[OSD([sQuery(id+"F18.wireOp",EDGE,"E27"),sQuery(id+"F18.wireOp",EDGE,"E28"),sQuery(id+"F18.wireOp",EDGE,"E29"),sQuery(id+"F18.wireOp",EDGE,"E30.trimOffspring")])]});
            var Q8;
            Q8=makeQuery(id+"F23.opPattern","COPY",BODY,{"derivedFrom":makeQuery(id+"F19.opExtrude","SWEPT_BODY",BODY,{"disambiguationData":[OSD([sQuery(id+"F18.wireOp",EDGE,"E27"),sQuery(id+"F18.wireOp",EDGE,"E28"),sQuery(id+"F18.wireOp",EDGE,"E29"),sQuery(id+"F18.wireOp",EDGE,"E30.trimOffspring")])]}),"instanceName":"9"});
            var Q9;
            Q9=makeQuery(id+"F23.opPattern","COPY",BODY,{"derivedFrom":makeQuery(id+"F19.opExtrude","SWEPT_BODY",BODY,{"disambiguationData":[OSD([sQuery(id+"F18.wireOp",EDGE,"E27"),sQuery(id+"F18.wireOp",EDGE,"E28"),sQuery(id+"F18.wireOp",EDGE,"E29"),sQuery(id+"F18.wireOp",EDGE,"E30.trimOffspring")])]}),"instanceName":"2"});
            var Q10;
            Q10=makeQuery(id+"F23.opPattern","COPY",BODY,{"derivedFrom":makeQuery(id+"F19.opExtrude","SWEPT_BODY",BODY,{"disambiguationData":[OSD([sQuery(id+"F18.wireOp",EDGE,"E27"),sQuery(id+"F18.wireOp",EDGE,"E28"),sQuery(id+"F18.wireOp",EDGE,"E29"),sQuery(id+"F18.wireOp",EDGE,"E30.trimOffspring")])]}),"instanceName":"8"});
            var Q11;
            Q11=makeQuery(id+"F1.opRevolve","SWEPT_BODY",BODY,{"disambiguationData":[OSD([sQuery(id+"F0.wireOp",EDGE,"E0.bottom"),sQuery(id+"F0.wireOp",EDGE,"E0.top"),sQuery(id+"F0.wireOp",EDGE,"E0.left"),sQuery(id+"F0.wireOp",EDGE,"E0.right")])]});
            booleanBodies(context, id + "F25", {"operationType" : BooleanOperationType.UNION, "tools" : qUnion([Q0, Q1, Q2, Q3, Q4, Q5, Q6, Q7, Q8, Q9, Q10, Q11])});
        }
        {
            var Q0;
            {var subQ0=sQuery(id+"F11.wireOp",EDGE,"E18.filletArc");var subQ1=sQuery(id+"F11.wireOp",EDGE,"E11");var subQ3=makeQuery(id+"F12.opExtrude","SWEPT_FACE",FACE,{"disambiguationData":[OSD([subQ1])]});var subQ4=sQuery(id+"F18.wireOp",EDGE,"E28");Q0=makeQuery(id+"F25.opBoolean","INTERSECT",EDGE,{"derivedFrom":[makeQuery(id+"F23.opPattern","COPY",FACE,{"derivedFrom":makeQuery(id+"F21.opBoolean","MERGE",FACE,{"derivedFrom":[makeQuery(id+"F19.opExtrude","SWEPT_FACE",FACE,{"disambiguationData":[OSD([subQ4])]}),makeQuery(id+"F20.opExtrude","SWEPT_FACE",FACE,{"disambiguationData":[OSD([subQ4])]})]}),"instanceName":"5"}),makeQuery(id+"F24.opBoolean","SPLIT",FACE,{"disambiguationData":[TD([makeQuery(id+"F16.opBoolean","COPY",FACE,{"derivedFrom":makeQuery(id+"F15.opPattern","COPY",FACE,{"derivedFrom":makeQuery(id+"F13.opPattern","COPY",FACE,{"derivedFrom":makeQuery(id+"F12.opExtrude","SWEPT_FACE",FACE,{"disambiguationData":[OSD([subQ0])]}),"instanceName":"4"}),"instanceName":"1"})})])],"derivedFrom":makeQuery(id+"F16.opBoolean","MERGE",FACE,{"derivedFrom":[makeQuery(id+"F14.opBoolean","COPY",FACE,{"derivedFrom":makeQuery(id+"F13.opPattern","COPY",FACE,{"derivedFrom":subQ3,"instanceName":"1"})}),makeQuery(id+"F14.opBoolean","COPY",FACE,{"derivedFrom":makeQuery(id+"F13.opPattern","COPY",FACE,{"derivedFrom":subQ3,"instanceName":"3"})}),makeQuery(id+"F14.opBoolean","COPY",FACE,{"derivedFrom":makeQuery(id+"F13.opPattern","COPY",FACE,{"derivedFrom":subQ3,"instanceName":"5"})}),makeQuery(id+"F14.opBoolean","COPY",FACE,{"derivedFrom":makeQuery(id+"F13.opPattern","COPY",FACE,{"derivedFrom":subQ3,"instanceName":"7"})}),makeQuery(id+"F14.opBoolean","COPY",FACE,{"derivedFrom":makeQuery(id+"F13.opPattern","COPY",FACE,{"derivedFrom":subQ3,"instanceName":"9"})})],"fromTools":[makeQuery(id+"F15.opPattern","COPY",FACE,{"derivedFrom":subQ3,"instanceName":"1"}),makeQuery(id+"F15.opPattern","COPY",FACE,{"derivedFrom":makeQuery(id+"F13.opPattern","COPY",FACE,{"derivedFrom":subQ3,"instanceName":"2"}),"instanceName":"1"}),makeQuery(id+"F15.opPattern","COPY",FACE,{"derivedFrom":makeQuery(id+"F13.opPattern","COPY",FACE,{"derivedFrom":subQ3,"instanceName":"4"}),"instanceName":"1"}),makeQuery(id+"F15.opPattern","COPY",FACE,{"derivedFrom":makeQuery(id+"F13.opPattern","COPY",FACE,{"derivedFrom":subQ3,"instanceName":"6"}),"instanceName":"1"}),makeQuery(id+"F15.opPattern","COPY",FACE,{"derivedFrom":makeQuery(id+"F13.opPattern","COPY",FACE,{"derivedFrom":subQ3,"instanceName":"8"}),"instanceName":"1"})]})})]});}
            var Q1;
            {var subQ0=sQuery(id+"F11.wireOp",EDGE,"E18.filletArc");var subQ2=sQuery(id+"F11.wireOp",EDGE,"E11");var subQ4=makeQuery(id+"F12.opExtrude","SWEPT_FACE",FACE,{"disambiguationData":[OSD([subQ2])]});var subQ5=sQuery(id+"F18.wireOp",EDGE,"E28");Q1=makeQuery(id+"F25.opBoolean","INTERSECT",EDGE,{"derivedFrom":[makeQuery(id+"F23.opPattern","COPY",FACE,{"derivedFrom":makeQuery(id+"F21.opBoolean","MERGE",FACE,{"derivedFrom":[makeQuery(id+"F19.opExtrude","SWEPT_FACE",FACE,{"disambiguationData":[OSD([subQ5])]}),makeQuery(id+"F20.opExtrude","SWEPT_FACE",FACE,{"disambiguationData":[OSD([subQ5])]})]}),"instanceName":"4"}),makeQuery(id+"F24.opBoolean","SPLIT",FACE,{"disambiguationData":[TD([makeQuery(id+"F14.opBoolean","COPY",FACE,{"derivedFrom":makeQuery(id+"F13.opPattern","COPY",FACE,{"derivedFrom":makeQuery(id+"F12.opExtrude","SWEPT_FACE",FACE,{"disambiguationData":[OSD([subQ0])]}),"instanceName":"3"})})])],"derivedFrom":makeQuery(id+"F16.opBoolean","MERGE",FACE,{"derivedFrom":[makeQuery(id+"F14.opBoolean","COPY",FACE,{"derivedFrom":makeQuery(id+"F13.opPattern","COPY",FACE,{"derivedFrom":subQ4,"instanceName":"1"})}),makeQuery(id+"F14.opBoolean","COPY",FACE,{"derivedFrom":makeQuery(id+"F13.opPattern","COPY",FACE,{"derivedFrom":subQ4,"instanceName":"3"})}),makeQuery(id+"F14.opBoolean","COPY",FACE,{"derivedFrom":makeQuery(id+"F13.opPattern","COPY",FACE,{"derivedFrom":subQ4,"instanceName":"5"})}),makeQuery(id+"F14.opBoolean","COPY",FACE,{"derivedFrom":makeQuery(id+"F13.opPattern","COPY",FACE,{"derivedFrom":subQ4,"instanceName":"7"})}),makeQuery(id+"F14.opBoolean","COPY",FACE,{"derivedFrom":makeQuery(id+"F13.opPattern","COPY",FACE,{"derivedFrom":subQ4,"instanceName":"9"})})],"fromTools":[makeQuery(id+"F15.opPattern","COPY",FACE,{"derivedFrom":subQ4,"instanceName":"1"}),makeQuery(id+"F15.opPattern","COPY",FACE,{"derivedFrom":makeQuery(id+"F13.opPattern","COPY",FACE,{"derivedFrom":subQ4,"instanceName":"2"}),"instanceName":"1"}),makeQuery(id+"F15.opPattern","COPY",FACE,{"derivedFrom":makeQuery(id+"F13.opPattern","COPY",FACE,{"derivedFrom":subQ4,"instanceName":"4"}),"instanceName":"1"}),makeQuery(id+"F15.opPattern","COPY",FACE,{"derivedFrom":makeQuery(id+"F13.opPattern","COPY",FACE,{"derivedFrom":subQ4,"instanceName":"6"}),"instanceName":"1"}),makeQuery(id+"F15.opPattern","COPY",FACE,{"derivedFrom":makeQuery(id+"F13.opPattern","COPY",FACE,{"derivedFrom":subQ4,"instanceName":"8"}),"instanceName":"1"})]})})]});}
            var Q2;
            {var subQ0=sQuery(id+"F11.wireOp",EDGE,"E18.filletArc");var subQ2=sQuery(id+"F11.wireOp",EDGE,"E11");var subQ4=makeQuery(id+"F12.opExtrude","SWEPT_FACE",FACE,{"disambiguationData":[OSD([subQ2])]});var subQ5=sQuery(id+"F18.wireOp",EDGE,"E28");Q2=makeQuery(id+"F25.opBoolean","INTERSECT",EDGE,{"derivedFrom":[makeQuery(id+"F23.opPattern","COPY",FACE,{"derivedFrom":makeQuery(id+"F21.opBoolean","MERGE",FACE,{"derivedFrom":[makeQuery(id+"F19.opExtrude","SWEPT_FACE",FACE,{"disambiguationData":[OSD([subQ5])]}),makeQuery(id+"F20.opExtrude","SWEPT_FACE",FACE,{"disambiguationData":[OSD([subQ5])]})]}),"instanceName":"4"}),makeQuery(id+"F24.opBoolean","SPLIT",FACE,{"disambiguationData":[TD([makeQuery(id+"F16.opBoolean","COPY",FACE,{"derivedFrom":makeQuery(id+"F15.opPattern","COPY",FACE,{"derivedFrom":makeQuery(id+"F13.opPattern","COPY",FACE,{"derivedFrom":makeQuery(id+"F12.opExtrude","SWEPT_FACE",FACE,{"disambiguationData":[OSD([subQ0])]}),"instanceName":"2"}),"instanceName":"1"})})])],"derivedFrom":makeQuery(id+"F16.opBoolean","MERGE",FACE,{"derivedFrom":[makeQuery(id+"F14.opBoolean","COPY",FACE,{"derivedFrom":makeQuery(id+"F13.opPattern","COPY",FACE,{"derivedFrom":subQ4,"instanceName":"1"})}),makeQuery(id+"F14.opBoolean","COPY",FACE,{"derivedFrom":makeQuery(id+"F13.opPattern","COPY",FACE,{"derivedFrom":subQ4,"instanceName":"3"})}),makeQuery(id+"F14.opBoolean","COPY",FACE,{"derivedFrom":makeQuery(id+"F13.opPattern","COPY",FACE,{"derivedFrom":subQ4,"instanceName":"5"})}),makeQuery(id+"F14.opBoolean","COPY",FACE,{"derivedFrom":makeQuery(id+"F13.opPattern","COPY",FACE,{"derivedFrom":subQ4,"instanceName":"7"})}),makeQuery(id+"F14.opBoolean","COPY",FACE,{"derivedFrom":makeQuery(id+"F13.opPattern","COPY",FACE,{"derivedFrom":subQ4,"instanceName":"9"})})],"fromTools":[makeQuery(id+"F15.opPattern","COPY",FACE,{"derivedFrom":subQ4,"instanceName":"1"}),makeQuery(id+"F15.opPattern","COPY",FACE,{"derivedFrom":makeQuery(id+"F13.opPattern","COPY",FACE,{"derivedFrom":subQ4,"instanceName":"2"}),"instanceName":"1"}),makeQuery(id+"F15.opPattern","COPY",FACE,{"derivedFrom":makeQuery(id+"F13.opPattern","COPY",FACE,{"derivedFrom":subQ4,"instanceName":"4"}),"instanceName":"1"}),makeQuery(id+"F15.opPattern","COPY",FACE,{"derivedFrom":makeQuery(id+"F13.opPattern","COPY",FACE,{"derivedFrom":subQ4,"instanceName":"6"}),"instanceName":"1"}),makeQuery(id+"F15.opPattern","COPY",FACE,{"derivedFrom":makeQuery(id+"F13.opPattern","COPY",FACE,{"derivedFrom":subQ4,"instanceName":"8"}),"instanceName":"1"})]})})]});}
            var Q3;
            {var subQ0=sQuery(id+"F11.wireOp",EDGE,"E18.filletArc");var subQ2=sQuery(id+"F11.wireOp",EDGE,"E11");var subQ4=makeQuery(id+"F12.opExtrude","SWEPT_FACE",FACE,{"disambiguationData":[OSD([subQ2])]});var subQ5=sQuery(id+"F18.wireOp",EDGE,"E28");Q3=makeQuery(id+"F25.opBoolean","INTERSECT",EDGE,{"derivedFrom":[makeQuery(id+"F23.opPattern","COPY",FACE,{"derivedFrom":makeQuery(id+"F21.opBoolean","MERGE",FACE,{"derivedFrom":[makeQuery(id+"F19.opExtrude","SWEPT_FACE",FACE,{"disambiguationData":[OSD([subQ5])]}),makeQuery(id+"F20.opExtrude","SWEPT_FACE",FACE,{"disambiguationData":[OSD([subQ5])]})]}),"instanceName":"3"}),makeQuery(id+"F24.opBoolean","SPLIT",FACE,{"disambiguationData":[TD([makeQuery(id+"F16.opBoolean","COPY",FACE,{"derivedFrom":makeQuery(id+"F15.opPattern","COPY",FACE,{"derivedFrom":makeQuery(id+"F13.opPattern","COPY",FACE,{"derivedFrom":makeQuery(id+"F12.opExtrude","SWEPT_FACE",FACE,{"disambiguationData":[OSD([subQ0])]}),"instanceName":"2"}),"instanceName":"1"})})])],"derivedFrom":makeQuery(id+"F16.opBoolean","MERGE",FACE,{"derivedFrom":[makeQuery(id+"F14.opBoolean","COPY",FACE,{"derivedFrom":makeQuery(id+"F13.opPattern","COPY",FACE,{"derivedFrom":subQ4,"instanceName":"1"})}),makeQuery(id+"F14.opBoolean","COPY",FACE,{"derivedFrom":makeQuery(id+"F13.opPattern","COPY",FACE,{"derivedFrom":subQ4,"instanceName":"3"})}),makeQuery(id+"F14.opBoolean","COPY",FACE,{"derivedFrom":makeQuery(id+"F13.opPattern","COPY",FACE,{"derivedFrom":subQ4,"instanceName":"5"})}),makeQuery(id+"F14.opBoolean","COPY",FACE,{"derivedFrom":makeQuery(id+"F13.opPattern","COPY",FACE,{"derivedFrom":subQ4,"instanceName":"7"})}),makeQuery(id+"F14.opBoolean","COPY",FACE,{"derivedFrom":makeQuery(id+"F13.opPattern","COPY",FACE,{"derivedFrom":subQ4,"instanceName":"9"})})],"fromTools":[makeQuery(id+"F15.opPattern","COPY",FACE,{"derivedFrom":subQ4,"instanceName":"1"}),makeQuery(id+"F15.opPattern","COPY",FACE,{"derivedFrom":makeQuery(id+"F13.opPattern","COPY",FACE,{"derivedFrom":subQ4,"instanceName":"2"}),"instanceName":"1"}),makeQuery(id+"F15.opPattern","COPY",FACE,{"derivedFrom":makeQuery(id+"F13.opPattern","COPY",FACE,{"derivedFrom":subQ4,"instanceName":"4"}),"instanceName":"1"}),makeQuery(id+"F15.opPattern","COPY",FACE,{"derivedFrom":makeQuery(id+"F13.opPattern","COPY",FACE,{"derivedFrom":subQ4,"instanceName":"6"}),"instanceName":"1"}),makeQuery(id+"F15.opPattern","COPY",FACE,{"derivedFrom":makeQuery(id+"F13.opPattern","COPY",FACE,{"derivedFrom":subQ4,"instanceName":"8"}),"instanceName":"1"})]})})]});}
            var Q4;
            {var subQ0=sQuery(id+"F11.wireOp",EDGE,"E19.filletArc");var subQ1=sQuery(id+"F11.wireOp",EDGE,"E11");var subQ3=makeQuery(id+"F12.opExtrude","SWEPT_FACE",FACE,{"disambiguationData":[OSD([subQ1])]});var subQ4=sQuery(id+"F18.wireOp",EDGE,"E28");Q4=makeQuery(id+"F25.opBoolean","INTERSECT",EDGE,{"derivedFrom":[makeQuery(id+"F23.opPattern","COPY",FACE,{"derivedFrom":makeQuery(id+"F21.opBoolean","MERGE",FACE,{"derivedFrom":[makeQuery(id+"F19.opExtrude","SWEPT_FACE",FACE,{"disambiguationData":[OSD([subQ4])]}),makeQuery(id+"F20.opExtrude","SWEPT_FACE",FACE,{"disambiguationData":[OSD([subQ4])]})]}),"instanceName":"3"}),makeQuery(id+"F24.opBoolean","SPLIT",FACE,{"disambiguationData":[TD([makeQuery(id+"F14.opBoolean","COPY",FACE,{"derivedFrom":makeQuery(id+"F13.opPattern","COPY",FACE,{"derivedFrom":makeQuery(id+"F12.opExtrude","SWEPT_FACE",FACE,{"disambiguationData":[OSD([subQ0])]}),"instanceName":"3"})})])],"derivedFrom":makeQuery(id+"F16.opBoolean","MERGE",FACE,{"derivedFrom":[makeQuery(id+"F14.opBoolean","COPY",FACE,{"derivedFrom":makeQuery(id+"F13.opPattern","COPY",FACE,{"derivedFrom":subQ3,"instanceName":"1"})}),makeQuery(id+"F14.opBoolean","COPY",FACE,{"derivedFrom":makeQuery(id+"F13.opPattern","COPY",FACE,{"derivedFrom":subQ3,"instanceName":"3"})}),makeQuery(id+"F14.opBoolean","COPY",FACE,{"derivedFrom":makeQuery(id+"F13.opPattern","COPY",FACE,{"derivedFrom":subQ3,"instanceName":"5"})}),makeQuery(id+"F14.opBoolean","COPY",FACE,{"derivedFrom":makeQuery(id+"F13.opPattern","COPY",FACE,{"derivedFrom":subQ3,"instanceName":"7"})}),makeQuery(id+"F14.opBoolean","COPY",FACE,{"derivedFrom":makeQuery(id+"F13.opPattern","COPY",FACE,{"derivedFrom":subQ3,"instanceName":"9"})})],"fromTools":[makeQuery(id+"F15.opPattern","COPY",FACE,{"derivedFrom":subQ3,"instanceName":"1"}),makeQuery(id+"F15.opPattern","COPY",FACE,{"derivedFrom":makeQuery(id+"F13.opPattern","COPY",FACE,{"derivedFrom":subQ3,"instanceName":"2"}),"instanceName":"1"}),makeQuery(id+"F15.opPattern","COPY",FACE,{"derivedFrom":makeQuery(id+"F13.opPattern","COPY",FACE,{"derivedFrom":subQ3,"instanceName":"4"}),"instanceName":"1"}),makeQuery(id+"F15.opPattern","COPY",FACE,{"derivedFrom":makeQuery(id+"F13.opPattern","COPY",FACE,{"derivedFrom":subQ3,"instanceName":"6"}),"instanceName":"1"}),makeQuery(id+"F15.opPattern","COPY",FACE,{"derivedFrom":makeQuery(id+"F13.opPattern","COPY",FACE,{"derivedFrom":subQ3,"instanceName":"8"}),"instanceName":"1"})]})})]});}
            var Q5;
            {var subQ0=sQuery(id+"F11.wireOp",EDGE,"E19.filletArc");var subQ1=sQuery(id+"F11.wireOp",EDGE,"E11");var subQ3=makeQuery(id+"F12.opExtrude","SWEPT_FACE",FACE,{"disambiguationData":[OSD([subQ1])]});var subQ4=sQuery(id+"F18.wireOp",EDGE,"E28");Q5=makeQuery(id+"F25.opBoolean","INTERSECT",EDGE,{"derivedFrom":[makeQuery(id+"F23.opPattern","COPY",FACE,{"derivedFrom":makeQuery(id+"F21.opBoolean","MERGE",FACE,{"derivedFrom":[makeQuery(id+"F19.opExtrude","SWEPT_FACE",FACE,{"disambiguationData":[OSD([subQ4])]}),makeQuery(id+"F20.opExtrude","SWEPT_FACE",FACE,{"disambiguationData":[OSD([subQ4])]})]}),"instanceName":"2"}),makeQuery(id+"F24.opBoolean","SPLIT",FACE,{"disambiguationData":[TD([makeQuery(id+"F16.opBoolean","COPY",FACE,{"derivedFrom":makeQuery(id+"F15.opPattern","COPY",FACE,{"derivedFrom":makeQuery(id+"F13.opPattern","COPY",FACE,{"derivedFrom":makeQuery(id+"F12.opExtrude","SWEPT_FACE",FACE,{"disambiguationData":[OSD([subQ0])]}),"instanceName":"2"}),"instanceName":"1"})})])],"derivedFrom":makeQuery(id+"F16.opBoolean","MERGE",FACE,{"derivedFrom":[makeQuery(id+"F14.opBoolean","COPY",FACE,{"derivedFrom":makeQuery(id+"F13.opPattern","COPY",FACE,{"derivedFrom":subQ3,"instanceName":"1"})}),makeQuery(id+"F14.opBoolean","COPY",FACE,{"derivedFrom":makeQuery(id+"F13.opPattern","COPY",FACE,{"derivedFrom":subQ3,"instanceName":"3"})}),makeQuery(id+"F14.opBoolean","COPY",FACE,{"derivedFrom":makeQuery(id+"F13.opPattern","COPY",FACE,{"derivedFrom":subQ3,"instanceName":"5"})}),makeQuery(id+"F14.opBoolean","COPY",FACE,{"derivedFrom":makeQuery(id+"F13.opPattern","COPY",FACE,{"derivedFrom":subQ3,"instanceName":"7"})}),makeQuery(id+"F14.opBoolean","COPY",FACE,{"derivedFrom":makeQuery(id+"F13.opPattern","COPY",FACE,{"derivedFrom":subQ3,"instanceName":"9"})})],"fromTools":[makeQuery(id+"F15.opPattern","COPY",FACE,{"derivedFrom":subQ3,"instanceName":"1"}),makeQuery(id+"F15.opPattern","COPY",FACE,{"derivedFrom":makeQuery(id+"F13.opPattern","COPY",FACE,{"derivedFrom":subQ3,"instanceName":"2"}),"instanceName":"1"}),makeQuery(id+"F15.opPattern","COPY",FACE,{"derivedFrom":makeQuery(id+"F13.opPattern","COPY",FACE,{"derivedFrom":subQ3,"instanceName":"4"}),"instanceName":"1"}),makeQuery(id+"F15.opPattern","COPY",FACE,{"derivedFrom":makeQuery(id+"F13.opPattern","COPY",FACE,{"derivedFrom":subQ3,"instanceName":"6"}),"instanceName":"1"}),makeQuery(id+"F15.opPattern","COPY",FACE,{"derivedFrom":makeQuery(id+"F13.opPattern","COPY",FACE,{"derivedFrom":subQ3,"instanceName":"8"}),"instanceName":"1"})]})})]});}
            var Q6;
            {var subQ0=sQuery(id+"F11.wireOp",EDGE,"E19.filletArc");var subQ1=sQuery(id+"F11.wireOp",EDGE,"E11");var subQ3=makeQuery(id+"F12.opExtrude","SWEPT_FACE",FACE,{"disambiguationData":[OSD([subQ1])]});var subQ4=sQuery(id+"F18.wireOp",EDGE,"E28");Q6=makeQuery(id+"F25.opBoolean","INTERSECT",EDGE,{"derivedFrom":[makeQuery(id+"F23.opPattern","COPY",FACE,{"derivedFrom":makeQuery(id+"F21.opBoolean","MERGE",FACE,{"derivedFrom":[makeQuery(id+"F19.opExtrude","SWEPT_FACE",FACE,{"disambiguationData":[OSD([subQ4])]}),makeQuery(id+"F20.opExtrude","SWEPT_FACE",FACE,{"disambiguationData":[OSD([subQ4])]})]}),"instanceName":"1"}),makeQuery(id+"F24.opBoolean","SPLIT",FACE,{"disambiguationData":[TD([makeQuery(id+"F16.opBoolean","COPY",FACE,{"derivedFrom":makeQuery(id+"F15.opPattern","COPY",FACE,{"derivedFrom":makeQuery(id+"F13.opPattern","COPY",FACE,{"derivedFrom":makeQuery(id+"F12.opExtrude","SWEPT_FACE",FACE,{"disambiguationData":[OSD([subQ0])]}),"instanceName":"2"}),"instanceName":"1"})})])],"derivedFrom":makeQuery(id+"F16.opBoolean","MERGE",FACE,{"derivedFrom":[makeQuery(id+"F14.opBoolean","COPY",FACE,{"derivedFrom":makeQuery(id+"F13.opPattern","COPY",FACE,{"derivedFrom":subQ3,"instanceName":"1"})}),makeQuery(id+"F14.opBoolean","COPY",FACE,{"derivedFrom":makeQuery(id+"F13.opPattern","COPY",FACE,{"derivedFrom":subQ3,"instanceName":"3"})}),makeQuery(id+"F14.opBoolean","COPY",FACE,{"derivedFrom":makeQuery(id+"F13.opPattern","COPY",FACE,{"derivedFrom":subQ3,"instanceName":"5"})}),makeQuery(id+"F14.opBoolean","COPY",FACE,{"derivedFrom":makeQuery(id+"F13.opPattern","COPY",FACE,{"derivedFrom":subQ3,"instanceName":"7"})}),makeQuery(id+"F14.opBoolean","COPY",FACE,{"derivedFrom":makeQuery(id+"F13.opPattern","COPY",FACE,{"derivedFrom":subQ3,"instanceName":"9"})})],"fromTools":[makeQuery(id+"F15.opPattern","COPY",FACE,{"derivedFrom":subQ3,"instanceName":"1"}),makeQuery(id+"F15.opPattern","COPY",FACE,{"derivedFrom":makeQuery(id+"F13.opPattern","COPY",FACE,{"derivedFrom":subQ3,"instanceName":"2"}),"instanceName":"1"}),makeQuery(id+"F15.opPattern","COPY",FACE,{"derivedFrom":makeQuery(id+"F13.opPattern","COPY",FACE,{"derivedFrom":subQ3,"instanceName":"4"}),"instanceName":"1"}),makeQuery(id+"F15.opPattern","COPY",FACE,{"derivedFrom":makeQuery(id+"F13.opPattern","COPY",FACE,{"derivedFrom":subQ3,"instanceName":"6"}),"instanceName":"1"}),makeQuery(id+"F15.opPattern","COPY",FACE,{"derivedFrom":makeQuery(id+"F13.opPattern","COPY",FACE,{"derivedFrom":subQ3,"instanceName":"8"}),"instanceName":"1"})]})})]});}
            var Q7;
            {var subQ0=sQuery(id+"F11.wireOp",EDGE,"E19.filletArc");var subQ1=sQuery(id+"F11.wireOp",EDGE,"E11");var subQ3=makeQuery(id+"F12.opExtrude","SWEPT_FACE",FACE,{"disambiguationData":[OSD([subQ1])]});var subQ4=sQuery(id+"F18.wireOp",EDGE,"E28");Q7=makeQuery(id+"F25.opBoolean","INTERSECT",EDGE,{"derivedFrom":[makeQuery(id+"F23.opPattern","COPY",FACE,{"derivedFrom":makeQuery(id+"F21.opBoolean","MERGE",FACE,{"derivedFrom":[makeQuery(id+"F19.opExtrude","SWEPT_FACE",FACE,{"disambiguationData":[OSD([subQ4])]}),makeQuery(id+"F20.opExtrude","SWEPT_FACE",FACE,{"disambiguationData":[OSD([subQ4])]})]}),"instanceName":"1"}),makeQuery(id+"F24.opBoolean","SPLIT",FACE,{"disambiguationData":[TD([makeQuery(id+"F14.opBoolean","COPY",FACE,{"derivedFrom":makeQuery(id+"F13.opPattern","COPY",FACE,{"derivedFrom":makeQuery(id+"F12.opExtrude","SWEPT_FACE",FACE,{"disambiguationData":[OSD([subQ0])]}),"instanceName":"1"})})])],"derivedFrom":makeQuery(id+"F16.opBoolean","MERGE",FACE,{"derivedFrom":[makeQuery(id+"F14.opBoolean","COPY",FACE,{"derivedFrom":makeQuery(id+"F13.opPattern","COPY",FACE,{"derivedFrom":subQ3,"instanceName":"1"})}),makeQuery(id+"F14.opBoolean","COPY",FACE,{"derivedFrom":makeQuery(id+"F13.opPattern","COPY",FACE,{"derivedFrom":subQ3,"instanceName":"3"})}),makeQuery(id+"F14.opBoolean","COPY",FACE,{"derivedFrom":makeQuery(id+"F13.opPattern","COPY",FACE,{"derivedFrom":subQ3,"instanceName":"5"})}),makeQuery(id+"F14.opBoolean","COPY",FACE,{"derivedFrom":makeQuery(id+"F13.opPattern","COPY",FACE,{"derivedFrom":subQ3,"instanceName":"7"})}),makeQuery(id+"F14.opBoolean","COPY",FACE,{"derivedFrom":makeQuery(id+"F13.opPattern","COPY",FACE,{"derivedFrom":subQ3,"instanceName":"9"})})],"fromTools":[makeQuery(id+"F15.opPattern","COPY",FACE,{"derivedFrom":subQ3,"instanceName":"1"}),makeQuery(id+"F15.opPattern","COPY",FACE,{"derivedFrom":makeQuery(id+"F13.opPattern","COPY",FACE,{"derivedFrom":subQ3,"instanceName":"2"}),"instanceName":"1"}),makeQuery(id+"F15.opPattern","COPY",FACE,{"derivedFrom":makeQuery(id+"F13.opPattern","COPY",FACE,{"derivedFrom":subQ3,"instanceName":"4"}),"instanceName":"1"}),makeQuery(id+"F15.opPattern","COPY",FACE,{"derivedFrom":makeQuery(id+"F13.opPattern","COPY",FACE,{"derivedFrom":subQ3,"instanceName":"6"}),"instanceName":"1"}),makeQuery(id+"F15.opPattern","COPY",FACE,{"derivedFrom":makeQuery(id+"F13.opPattern","COPY",FACE,{"derivedFrom":subQ3,"instanceName":"8"}),"instanceName":"1"})]})})]});}
            var Q8;
            {var subQ0=sQuery(id+"F11.wireOp",EDGE,"E18.filletArc");var subQ2=sQuery(id+"F11.wireOp",EDGE,"E11");var subQ5=makeQuery(id+"F12.opExtrude","SWEPT_FACE",FACE,{"disambiguationData":[OSD([subQ2])]});var subQ6=sQuery(id+"F18.wireOp",EDGE,"E28");Q8=makeQuery(id+"F25.opBoolean","INTERSECT",EDGE,{"derivedFrom":[makeQuery(id+"F23.opPattern","COPY",FACE,{"derivedFrom":makeQuery(id+"F21.opBoolean","MERGE",FACE,{"derivedFrom":[makeQuery(id+"F19.opExtrude","SWEPT_FACE",FACE,{"disambiguationData":[OSD([subQ6])]}),makeQuery(id+"F20.opExtrude","SWEPT_FACE",FACE,{"disambiguationData":[OSD([subQ6])]})]}),"instanceName":"10"}),makeQuery(id+"F24.opBoolean","SPLIT",FACE,{"disambiguationData":[TD([makeQuery(id+"F14.opBoolean","COPY",FACE,{"derivedFrom":makeQuery(id+"F13.opPattern","COPY",FACE,{"derivedFrom":makeQuery(id+"F12.opExtrude","SWEPT_FACE",FACE,{"disambiguationData":[OSD([subQ0])]}),"instanceName":"9"})})])],"derivedFrom":makeQuery(id+"F16.opBoolean","MERGE",FACE,{"derivedFrom":[makeQuery(id+"F14.opBoolean","COPY",FACE,{"derivedFrom":makeQuery(id+"F13.opPattern","COPY",FACE,{"derivedFrom":subQ5,"instanceName":"1"})}),makeQuery(id+"F14.opBoolean","COPY",FACE,{"derivedFrom":makeQuery(id+"F13.opPattern","COPY",FACE,{"derivedFrom":subQ5,"instanceName":"3"})}),makeQuery(id+"F14.opBoolean","COPY",FACE,{"derivedFrom":makeQuery(id+"F13.opPattern","COPY",FACE,{"derivedFrom":subQ5,"instanceName":"5"})}),makeQuery(id+"F14.opBoolean","COPY",FACE,{"derivedFrom":makeQuery(id+"F13.opPattern","COPY",FACE,{"derivedFrom":subQ5,"instanceName":"7"})}),makeQuery(id+"F14.opBoolean","COPY",FACE,{"derivedFrom":makeQuery(id+"F13.opPattern","COPY",FACE,{"derivedFrom":subQ5,"instanceName":"9"})})],"fromTools":[makeQuery(id+"F15.opPattern","COPY",FACE,{"derivedFrom":subQ5,"instanceName":"1"}),makeQuery(id+"F15.opPattern","COPY",FACE,{"derivedFrom":makeQuery(id+"F13.opPattern","COPY",FACE,{"derivedFrom":subQ5,"instanceName":"2"}),"instanceName":"1"}),makeQuery(id+"F15.opPattern","COPY",FACE,{"derivedFrom":makeQuery(id+"F13.opPattern","COPY",FACE,{"derivedFrom":subQ5,"instanceName":"4"}),"instanceName":"1"}),makeQuery(id+"F15.opPattern","COPY",FACE,{"derivedFrom":makeQuery(id+"F13.opPattern","COPY",FACE,{"derivedFrom":subQ5,"instanceName":"6"}),"instanceName":"1"}),makeQuery(id+"F15.opPattern","COPY",FACE,{"derivedFrom":makeQuery(id+"F13.opPattern","COPY",FACE,{"derivedFrom":subQ5,"instanceName":"8"}),"instanceName":"1"})]})})]});}
            var Q9;
            {var subQ0=sQuery(id+"F11.wireOp",EDGE,"E19.filletArc");var subQ2=sQuery(id+"F11.wireOp",EDGE,"E11");var subQ5=makeQuery(id+"F12.opExtrude","SWEPT_FACE",FACE,{"disambiguationData":[OSD([subQ2])]});var subQ6=sQuery(id+"F18.wireOp",EDGE,"E28");Q9=makeQuery(id+"F25.opBoolean","INTERSECT",EDGE,{"derivedFrom":[makeQuery(id+"F23.opPattern","COPY",FACE,{"derivedFrom":makeQuery(id+"F21.opBoolean","MERGE",FACE,{"derivedFrom":[makeQuery(id+"F19.opExtrude","SWEPT_FACE",FACE,{"disambiguationData":[OSD([subQ6])]}),makeQuery(id+"F20.opExtrude","SWEPT_FACE",FACE,{"disambiguationData":[OSD([subQ6])]})]}),"instanceName":"10"}),makeQuery(id+"F24.opBoolean","SPLIT",FACE,{"disambiguationData":[TD([makeQuery(id+"F14.opBoolean","COPY",FACE,{"derivedFrom":makeQuery(id+"F13.opPattern","COPY",FACE,{"derivedFrom":makeQuery(id+"F12.opExtrude","SWEPT_FACE",FACE,{"disambiguationData":[OSD([subQ0])]}),"instanceName":"9"})})])],"derivedFrom":makeQuery(id+"F16.opBoolean","MERGE",FACE,{"derivedFrom":[makeQuery(id+"F14.opBoolean","COPY",FACE,{"derivedFrom":makeQuery(id+"F13.opPattern","COPY",FACE,{"derivedFrom":subQ5,"instanceName":"1"})}),makeQuery(id+"F14.opBoolean","COPY",FACE,{"derivedFrom":makeQuery(id+"F13.opPattern","COPY",FACE,{"derivedFrom":subQ5,"instanceName":"3"})}),makeQuery(id+"F14.opBoolean","COPY",FACE,{"derivedFrom":makeQuery(id+"F13.opPattern","COPY",FACE,{"derivedFrom":subQ5,"instanceName":"5"})}),makeQuery(id+"F14.opBoolean","COPY",FACE,{"derivedFrom":makeQuery(id+"F13.opPattern","COPY",FACE,{"derivedFrom":subQ5,"instanceName":"7"})}),makeQuery(id+"F14.opBoolean","COPY",FACE,{"derivedFrom":makeQuery(id+"F13.opPattern","COPY",FACE,{"derivedFrom":subQ5,"instanceName":"9"})})],"fromTools":[makeQuery(id+"F15.opPattern","COPY",FACE,{"derivedFrom":subQ5,"instanceName":"1"}),makeQuery(id+"F15.opPattern","COPY",FACE,{"derivedFrom":makeQuery(id+"F13.opPattern","COPY",FACE,{"derivedFrom":subQ5,"instanceName":"2"}),"instanceName":"1"}),makeQuery(id+"F15.opPattern","COPY",FACE,{"derivedFrom":makeQuery(id+"F13.opPattern","COPY",FACE,{"derivedFrom":subQ5,"instanceName":"4"}),"instanceName":"1"}),makeQuery(id+"F15.opPattern","COPY",FACE,{"derivedFrom":makeQuery(id+"F13.opPattern","COPY",FACE,{"derivedFrom":subQ5,"instanceName":"6"}),"instanceName":"1"}),makeQuery(id+"F15.opPattern","COPY",FACE,{"derivedFrom":makeQuery(id+"F13.opPattern","COPY",FACE,{"derivedFrom":subQ5,"instanceName":"8"}),"instanceName":"1"})]})})]});}
            var Q10;
            {var subQ0=sQuery(id+"F11.wireOp",EDGE,"E18.filletArc");var subQ1=sQuery(id+"F11.wireOp",EDGE,"E11");var subQ3=makeQuery(id+"F12.opExtrude","SWEPT_FACE",FACE,{"disambiguationData":[OSD([subQ1])]});var subQ4=sQuery(id+"F18.wireOp",EDGE,"E28");Q10=makeQuery(id+"F25.opBoolean","INTERSECT",EDGE,{"derivedFrom":[makeQuery(id+"F23.opPattern","COPY",FACE,{"derivedFrom":makeQuery(id+"F21.opBoolean","MERGE",FACE,{"derivedFrom":[makeQuery(id+"F19.opExtrude","SWEPT_FACE",FACE,{"disambiguationData":[OSD([subQ4])]}),makeQuery(id+"F20.opExtrude","SWEPT_FACE",FACE,{"disambiguationData":[OSD([subQ4])]})]}),"instanceName":"8"}),makeQuery(id+"F24.opBoolean","SPLIT",FACE,{"disambiguationData":[TD([makeQuery(id+"F14.opBoolean","COPY",FACE,{"derivedFrom":makeQuery(id+"F13.opPattern","COPY",FACE,{"derivedFrom":makeQuery(id+"F12.opExtrude","SWEPT_FACE",FACE,{"disambiguationData":[OSD([subQ0])]}),"instanceName":"7"})})])],"derivedFrom":makeQuery(id+"F16.opBoolean","MERGE",FACE,{"derivedFrom":[makeQuery(id+"F14.opBoolean","COPY",FACE,{"derivedFrom":makeQuery(id+"F13.opPattern","COPY",FACE,{"derivedFrom":subQ3,"instanceName":"1"})}),makeQuery(id+"F14.opBoolean","COPY",FACE,{"derivedFrom":makeQuery(id+"F13.opPattern","COPY",FACE,{"derivedFrom":subQ3,"instanceName":"3"})}),makeQuery(id+"F14.opBoolean","COPY",FACE,{"derivedFrom":makeQuery(id+"F13.opPattern","COPY",FACE,{"derivedFrom":subQ3,"instanceName":"5"})}),makeQuery(id+"F14.opBoolean","COPY",FACE,{"derivedFrom":makeQuery(id+"F13.opPattern","COPY",FACE,{"derivedFrom":subQ3,"instanceName":"7"})}),makeQuery(id+"F14.opBoolean","COPY",FACE,{"derivedFrom":makeQuery(id+"F13.opPattern","COPY",FACE,{"derivedFrom":subQ3,"instanceName":"9"})})],"fromTools":[makeQuery(id+"F15.opPattern","COPY",FACE,{"derivedFrom":subQ3,"instanceName":"1"}),makeQuery(id+"F15.opPattern","COPY",FACE,{"derivedFrom":makeQuery(id+"F13.opPattern","COPY",FACE,{"derivedFrom":subQ3,"instanceName":"2"}),"instanceName":"1"}),makeQuery(id+"F15.opPattern","COPY",FACE,{"derivedFrom":makeQuery(id+"F13.opPattern","COPY",FACE,{"derivedFrom":subQ3,"instanceName":"4"}),"instanceName":"1"}),makeQuery(id+"F15.opPattern","COPY",FACE,{"derivedFrom":makeQuery(id+"F13.opPattern","COPY",FACE,{"derivedFrom":subQ3,"instanceName":"6"}),"instanceName":"1"}),makeQuery(id+"F15.opPattern","COPY",FACE,{"derivedFrom":makeQuery(id+"F13.opPattern","COPY",FACE,{"derivedFrom":subQ3,"instanceName":"8"}),"instanceName":"1"})]})})]});}
            var Q11;
            {var subQ0=sQuery(id+"F11.wireOp",EDGE,"E18.filletArc");var subQ1=sQuery(id+"F11.wireOp",EDGE,"E11");var subQ3=makeQuery(id+"F12.opExtrude","SWEPT_FACE",FACE,{"disambiguationData":[OSD([subQ1])]});var subQ4=sQuery(id+"F18.wireOp",EDGE,"E28");Q11=makeQuery(id+"F25.opBoolean","INTERSECT",EDGE,{"derivedFrom":[makeQuery(id+"F23.opPattern","COPY",FACE,{"derivedFrom":makeQuery(id+"F21.opBoolean","MERGE",FACE,{"derivedFrom":[makeQuery(id+"F19.opExtrude","SWEPT_FACE",FACE,{"disambiguationData":[OSD([subQ4])]}),makeQuery(id+"F20.opExtrude","SWEPT_FACE",FACE,{"disambiguationData":[OSD([subQ4])]})]}),"instanceName":"8"}),makeQuery(id+"F24.opBoolean","SPLIT",FACE,{"disambiguationData":[TD([makeQuery(id+"F16.opBoolean","COPY",FACE,{"derivedFrom":makeQuery(id+"F15.opPattern","COPY",FACE,{"derivedFrom":makeQuery(id+"F13.opPattern","COPY",FACE,{"derivedFrom":makeQuery(id+"F12.opExtrude","SWEPT_FACE",FACE,{"disambiguationData":[OSD([subQ0])]}),"instanceName":"6"}),"instanceName":"1"})})])],"derivedFrom":makeQuery(id+"F16.opBoolean","MERGE",FACE,{"derivedFrom":[makeQuery(id+"F14.opBoolean","COPY",FACE,{"derivedFrom":makeQuery(id+"F13.opPattern","COPY",FACE,{"derivedFrom":subQ3,"instanceName":"1"})}),makeQuery(id+"F14.opBoolean","COPY",FACE,{"derivedFrom":makeQuery(id+"F13.opPattern","COPY",FACE,{"derivedFrom":subQ3,"instanceName":"3"})}),makeQuery(id+"F14.opBoolean","COPY",FACE,{"derivedFrom":makeQuery(id+"F13.opPattern","COPY",FACE,{"derivedFrom":subQ3,"instanceName":"5"})}),makeQuery(id+"F14.opBoolean","COPY",FACE,{"derivedFrom":makeQuery(id+"F13.opPattern","COPY",FACE,{"derivedFrom":subQ3,"instanceName":"7"})}),makeQuery(id+"F14.opBoolean","COPY",FACE,{"derivedFrom":makeQuery(id+"F13.opPattern","COPY",FACE,{"derivedFrom":subQ3,"instanceName":"9"})})],"fromTools":[makeQuery(id+"F15.opPattern","COPY",FACE,{"derivedFrom":subQ3,"instanceName":"1"}),makeQuery(id+"F15.opPattern","COPY",FACE,{"derivedFrom":makeQuery(id+"F13.opPattern","COPY",FACE,{"derivedFrom":subQ3,"instanceName":"2"}),"instanceName":"1"}),makeQuery(id+"F15.opPattern","COPY",FACE,{"derivedFrom":makeQuery(id+"F13.opPattern","COPY",FACE,{"derivedFrom":subQ3,"instanceName":"4"}),"instanceName":"1"}),makeQuery(id+"F15.opPattern","COPY",FACE,{"derivedFrom":makeQuery(id+"F13.opPattern","COPY",FACE,{"derivedFrom":subQ3,"instanceName":"6"}),"instanceName":"1"}),makeQuery(id+"F15.opPattern","COPY",FACE,{"derivedFrom":makeQuery(id+"F13.opPattern","COPY",FACE,{"derivedFrom":subQ3,"instanceName":"8"}),"instanceName":"1"})]})})]});}
            var Q12;
            {var subQ0=sQuery(id+"F11.wireOp",EDGE,"E18.filletArc");var subQ1=sQuery(id+"F11.wireOp",EDGE,"E11");var subQ3=makeQuery(id+"F12.opExtrude","SWEPT_FACE",FACE,{"disambiguationData":[OSD([subQ1])]});var subQ4=sQuery(id+"F18.wireOp",EDGE,"E28");Q12=makeQuery(id+"F25.opBoolean","INTERSECT",EDGE,{"derivedFrom":[makeQuery(id+"F23.opPattern","COPY",FACE,{"derivedFrom":makeQuery(id+"F21.opBoolean","MERGE",FACE,{"derivedFrom":[makeQuery(id+"F19.opExtrude","SWEPT_FACE",FACE,{"disambiguationData":[OSD([subQ4])]}),makeQuery(id+"F20.opExtrude","SWEPT_FACE",FACE,{"disambiguationData":[OSD([subQ4])]})]}),"instanceName":"7"}),makeQuery(id+"F24.opBoolean","SPLIT",FACE,{"disambiguationData":[TD([makeQuery(id+"F16.opBoolean","COPY",FACE,{"derivedFrom":makeQuery(id+"F15.opPattern","COPY",FACE,{"derivedFrom":makeQuery(id+"F13.opPattern","COPY",FACE,{"derivedFrom":makeQuery(id+"F12.opExtrude","SWEPT_FACE",FACE,{"disambiguationData":[OSD([subQ0])]}),"instanceName":"6"}),"instanceName":"1"})})])],"derivedFrom":makeQuery(id+"F16.opBoolean","MERGE",FACE,{"derivedFrom":[makeQuery(id+"F14.opBoolean","COPY",FACE,{"derivedFrom":makeQuery(id+"F13.opPattern","COPY",FACE,{"derivedFrom":subQ3,"instanceName":"1"})}),makeQuery(id+"F14.opBoolean","COPY",FACE,{"derivedFrom":makeQuery(id+"F13.opPattern","COPY",FACE,{"derivedFrom":subQ3,"instanceName":"3"})}),makeQuery(id+"F14.opBoolean","COPY",FACE,{"derivedFrom":makeQuery(id+"F13.opPattern","COPY",FACE,{"derivedFrom":subQ3,"instanceName":"5"})}),makeQuery(id+"F14.opBoolean","COPY",FACE,{"derivedFrom":makeQuery(id+"F13.opPattern","COPY",FACE,{"derivedFrom":subQ3,"instanceName":"7"})}),makeQuery(id+"F14.opBoolean","COPY",FACE,{"derivedFrom":makeQuery(id+"F13.opPattern","COPY",FACE,{"derivedFrom":subQ3,"instanceName":"9"})})],"fromTools":[makeQuery(id+"F15.opPattern","COPY",FACE,{"derivedFrom":subQ3,"instanceName":"1"}),makeQuery(id+"F15.opPattern","COPY",FACE,{"derivedFrom":makeQuery(id+"F13.opPattern","COPY",FACE,{"derivedFrom":subQ3,"instanceName":"2"}),"instanceName":"1"}),makeQuery(id+"F15.opPattern","COPY",FACE,{"derivedFrom":makeQuery(id+"F13.opPattern","COPY",FACE,{"derivedFrom":subQ3,"instanceName":"4"}),"instanceName":"1"}),makeQuery(id+"F15.opPattern","COPY",FACE,{"derivedFrom":makeQuery(id+"F13.opPattern","COPY",FACE,{"derivedFrom":subQ3,"instanceName":"6"}),"instanceName":"1"}),makeQuery(id+"F15.opPattern","COPY",FACE,{"derivedFrom":makeQuery(id+"F13.opPattern","COPY",FACE,{"derivedFrom":subQ3,"instanceName":"8"}),"instanceName":"1"})]})})]});}
            var Q13;
            {var subQ0=sQuery(id+"F11.wireOp",EDGE,"E18.filletArc");var subQ1=sQuery(id+"F11.wireOp",EDGE,"E11");var subQ3=makeQuery(id+"F12.opExtrude","SWEPT_FACE",FACE,{"disambiguationData":[OSD([subQ1])]});var subQ4=sQuery(id+"F18.wireOp",EDGE,"E28");Q13=makeQuery(id+"F25.opBoolean","INTERSECT",EDGE,{"derivedFrom":[makeQuery(id+"F23.opPattern","COPY",FACE,{"derivedFrom":makeQuery(id+"F21.opBoolean","MERGE",FACE,{"derivedFrom":[makeQuery(id+"F19.opExtrude","SWEPT_FACE",FACE,{"disambiguationData":[OSD([subQ4])]}),makeQuery(id+"F20.opExtrude","SWEPT_FACE",FACE,{"disambiguationData":[OSD([subQ4])]})]}),"instanceName":"6"}),makeQuery(id+"F24.opBoolean","SPLIT",FACE,{"disambiguationData":[TD([makeQuery(id+"F14.opBoolean","COPY",FACE,{"derivedFrom":makeQuery(id+"F13.opPattern","COPY",FACE,{"derivedFrom":makeQuery(id+"F12.opExtrude","SWEPT_FACE",FACE,{"disambiguationData":[OSD([subQ0])]}),"instanceName":"5"})})])],"derivedFrom":makeQuery(id+"F16.opBoolean","MERGE",FACE,{"derivedFrom":[makeQuery(id+"F14.opBoolean","COPY",FACE,{"derivedFrom":makeQuery(id+"F13.opPattern","COPY",FACE,{"derivedFrom":subQ3,"instanceName":"1"})}),makeQuery(id+"F14.opBoolean","COPY",FACE,{"derivedFrom":makeQuery(id+"F13.opPattern","COPY",FACE,{"derivedFrom":subQ3,"instanceName":"3"})}),makeQuery(id+"F14.opBoolean","COPY",FACE,{"derivedFrom":makeQuery(id+"F13.opPattern","COPY",FACE,{"derivedFrom":subQ3,"instanceName":"5"})}),makeQuery(id+"F14.opBoolean","COPY",FACE,{"derivedFrom":makeQuery(id+"F13.opPattern","COPY",FACE,{"derivedFrom":subQ3,"instanceName":"7"})}),makeQuery(id+"F14.opBoolean","COPY",FACE,{"derivedFrom":makeQuery(id+"F13.opPattern","COPY",FACE,{"derivedFrom":subQ3,"instanceName":"9"})})],"fromTools":[makeQuery(id+"F15.opPattern","COPY",FACE,{"derivedFrom":subQ3,"instanceName":"1"}),makeQuery(id+"F15.opPattern","COPY",FACE,{"derivedFrom":makeQuery(id+"F13.opPattern","COPY",FACE,{"derivedFrom":subQ3,"instanceName":"2"}),"instanceName":"1"}),makeQuery(id+"F15.opPattern","COPY",FACE,{"derivedFrom":makeQuery(id+"F13.opPattern","COPY",FACE,{"derivedFrom":subQ3,"instanceName":"4"}),"instanceName":"1"}),makeQuery(id+"F15.opPattern","COPY",FACE,{"derivedFrom":makeQuery(id+"F13.opPattern","COPY",FACE,{"derivedFrom":subQ3,"instanceName":"6"}),"instanceName":"1"}),makeQuery(id+"F15.opPattern","COPY",FACE,{"derivedFrom":makeQuery(id+"F13.opPattern","COPY",FACE,{"derivedFrom":subQ3,"instanceName":"8"}),"instanceName":"1"})]})})]});}
            var Q14;
            {var subQ0=sQuery(id+"F11.wireOp",EDGE,"E18.filletArc");var subQ1=sQuery(id+"F11.wireOp",EDGE,"E11");var subQ3=makeQuery(id+"F12.opExtrude","SWEPT_FACE",FACE,{"disambiguationData":[OSD([subQ1])]});var subQ4=sQuery(id+"F18.wireOp",EDGE,"E28");Q14=makeQuery(id+"F25.opBoolean","INTERSECT",EDGE,{"derivedFrom":[makeQuery(id+"F23.opPattern","COPY",FACE,{"derivedFrom":makeQuery(id+"F21.opBoolean","MERGE",FACE,{"derivedFrom":[makeQuery(id+"F19.opExtrude","SWEPT_FACE",FACE,{"disambiguationData":[OSD([subQ4])]}),makeQuery(id+"F20.opExtrude","SWEPT_FACE",FACE,{"disambiguationData":[OSD([subQ4])]})]}),"instanceName":"6"}),makeQuery(id+"F24.opBoolean","SPLIT",FACE,{"disambiguationData":[TD([makeQuery(id+"F16.opBoolean","COPY",FACE,{"derivedFrom":makeQuery(id+"F15.opPattern","COPY",FACE,{"derivedFrom":makeQuery(id+"F13.opPattern","COPY",FACE,{"derivedFrom":makeQuery(id+"F12.opExtrude","SWEPT_FACE",FACE,{"disambiguationData":[OSD([subQ0])]}),"instanceName":"4"}),"instanceName":"1"})})])],"derivedFrom":makeQuery(id+"F16.opBoolean","MERGE",FACE,{"derivedFrom":[makeQuery(id+"F14.opBoolean","COPY",FACE,{"derivedFrom":makeQuery(id+"F13.opPattern","COPY",FACE,{"derivedFrom":subQ3,"instanceName":"1"})}),makeQuery(id+"F14.opBoolean","COPY",FACE,{"derivedFrom":makeQuery(id+"F13.opPattern","COPY",FACE,{"derivedFrom":subQ3,"instanceName":"3"})}),makeQuery(id+"F14.opBoolean","COPY",FACE,{"derivedFrom":makeQuery(id+"F13.opPattern","COPY",FACE,{"derivedFrom":subQ3,"instanceName":"5"})}),makeQuery(id+"F14.opBoolean","COPY",FACE,{"derivedFrom":makeQuery(id+"F13.opPattern","COPY",FACE,{"derivedFrom":subQ3,"instanceName":"7"})}),makeQuery(id+"F14.opBoolean","COPY",FACE,{"derivedFrom":makeQuery(id+"F13.opPattern","COPY",FACE,{"derivedFrom":subQ3,"instanceName":"9"})})],"fromTools":[makeQuery(id+"F15.opPattern","COPY",FACE,{"derivedFrom":subQ3,"instanceName":"1"}),makeQuery(id+"F15.opPattern","COPY",FACE,{"derivedFrom":makeQuery(id+"F13.opPattern","COPY",FACE,{"derivedFrom":subQ3,"instanceName":"2"}),"instanceName":"1"}),makeQuery(id+"F15.opPattern","COPY",FACE,{"derivedFrom":makeQuery(id+"F13.opPattern","COPY",FACE,{"derivedFrom":subQ3,"instanceName":"4"}),"instanceName":"1"}),makeQuery(id+"F15.opPattern","COPY",FACE,{"derivedFrom":makeQuery(id+"F13.opPattern","COPY",FACE,{"derivedFrom":subQ3,"instanceName":"6"}),"instanceName":"1"}),makeQuery(id+"F15.opPattern","COPY",FACE,{"derivedFrom":makeQuery(id+"F13.opPattern","COPY",FACE,{"derivedFrom":subQ3,"instanceName":"8"}),"instanceName":"1"})]})})]});}
            var Q15;
            {var subQ0=sQuery(id+"F11.wireOp",EDGE,"E19.filletArc");var subQ1=sQuery(id+"F11.wireOp",EDGE,"E11");var subQ3=makeQuery(id+"F12.opExtrude","SWEPT_FACE",FACE,{"disambiguationData":[OSD([subQ1])]});var subQ4=sQuery(id+"F18.wireOp",EDGE,"E28");Q15=makeQuery(id+"F25.opBoolean","INTERSECT",EDGE,{"derivedFrom":[makeQuery(id+"F21.opBoolean","MERGE",FACE,{"derivedFrom":[makeQuery(id+"F19.opExtrude","SWEPT_FACE",FACE,{"disambiguationData":[OSD([subQ4])]}),makeQuery(id+"F20.opExtrude","SWEPT_FACE",FACE,{"disambiguationData":[OSD([subQ4])]})]}),makeQuery(id+"F24.opBoolean","SPLIT",FACE,{"disambiguationData":[TD([makeQuery(id+"F14.opBoolean","COPY",FACE,{"derivedFrom":makeQuery(id+"F13.opPattern","COPY",FACE,{"derivedFrom":makeQuery(id+"F12.opExtrude","SWEPT_FACE",FACE,{"disambiguationData":[OSD([subQ0])]}),"instanceName":"1"})})])],"derivedFrom":makeQuery(id+"F16.opBoolean","MERGE",FACE,{"derivedFrom":[makeQuery(id+"F14.opBoolean","COPY",FACE,{"derivedFrom":makeQuery(id+"F13.opPattern","COPY",FACE,{"derivedFrom":subQ3,"instanceName":"1"})}),makeQuery(id+"F14.opBoolean","COPY",FACE,{"derivedFrom":makeQuery(id+"F13.opPattern","COPY",FACE,{"derivedFrom":subQ3,"instanceName":"3"})}),makeQuery(id+"F14.opBoolean","COPY",FACE,{"derivedFrom":makeQuery(id+"F13.opPattern","COPY",FACE,{"derivedFrom":subQ3,"instanceName":"5"})}),makeQuery(id+"F14.opBoolean","COPY",FACE,{"derivedFrom":makeQuery(id+"F13.opPattern","COPY",FACE,{"derivedFrom":subQ3,"instanceName":"7"})}),makeQuery(id+"F14.opBoolean","COPY",FACE,{"derivedFrom":makeQuery(id+"F13.opPattern","COPY",FACE,{"derivedFrom":subQ3,"instanceName":"9"})})],"fromTools":[makeQuery(id+"F15.opPattern","COPY",FACE,{"derivedFrom":subQ3,"instanceName":"1"}),makeQuery(id+"F15.opPattern","COPY",FACE,{"derivedFrom":makeQuery(id+"F13.opPattern","COPY",FACE,{"derivedFrom":subQ3,"instanceName":"2"}),"instanceName":"1"}),makeQuery(id+"F15.opPattern","COPY",FACE,{"derivedFrom":makeQuery(id+"F13.opPattern","COPY",FACE,{"derivedFrom":subQ3,"instanceName":"4"}),"instanceName":"1"}),makeQuery(id+"F15.opPattern","COPY",FACE,{"derivedFrom":makeQuery(id+"F13.opPattern","COPY",FACE,{"derivedFrom":subQ3,"instanceName":"6"}),"instanceName":"1"}),makeQuery(id+"F15.opPattern","COPY",FACE,{"derivedFrom":makeQuery(id+"F13.opPattern","COPY",FACE,{"derivedFrom":subQ3,"instanceName":"8"}),"instanceName":"1"})]})})]});}
            var Q16;
            {var subQ0=sQuery(id+"F18.wireOp",EDGE,"E28");Q16=makeQuery(id+"F25.opBoolean","INTERSECT",EDGE,{"derivedFrom":[makeQuery(id+"F23.opPattern","COPY",FACE,{"derivedFrom":makeQuery(id+"F21.opBoolean","MERGE",FACE,{"derivedFrom":[makeQuery(id+"F19.opExtrude","SWEPT_FACE",FACE,{"disambiguationData":[OSD([subQ0])]}),makeQuery(id+"F20.opExtrude","SWEPT_FACE",FACE,{"disambiguationData":[OSD([subQ0])]})]}),"instanceName":"1"}),makeQuery(id+"F16.opBoolean","COPY",FACE,{"derivedFrom":makeQuery(id+"F15.opPattern","COPY",FACE,{"derivedFrom":makeQuery(id+"F12.opExtrude","SWEPT_FACE",FACE,{"disambiguationData":[OSD([sQuery(id+"F11.wireOp",EDGE,"E18.filletArc")])]}),"instanceName":"1"})})]});}
            var Q17;
            {var subQ0=sQuery(id+"F11.wireOp",EDGE,"E19.filletArc");var subQ1=sQuery(id+"F11.wireOp",EDGE,"E11");var subQ3=makeQuery(id+"F12.opExtrude","SWEPT_FACE",FACE,{"disambiguationData":[OSD([subQ1])]});var subQ4=sQuery(id+"F18.wireOp",EDGE,"E28");Q17=makeQuery(id+"F25.opBoolean","INTERSECT",EDGE,{"derivedFrom":[makeQuery(id+"F23.opPattern","COPY",FACE,{"derivedFrom":makeQuery(id+"F21.opBoolean","MERGE",FACE,{"derivedFrom":[makeQuery(id+"F19.opExtrude","SWEPT_FACE",FACE,{"disambiguationData":[OSD([subQ4])]}),makeQuery(id+"F20.opExtrude","SWEPT_FACE",FACE,{"disambiguationData":[OSD([subQ4])]})]}),"instanceName":"2"}),makeQuery(id+"F24.opBoolean","SPLIT",FACE,{"disambiguationData":[TD([makeQuery(id+"F14.opBoolean","COPY",FACE,{"derivedFrom":makeQuery(id+"F13.opPattern","COPY",FACE,{"derivedFrom":makeQuery(id+"F12.opExtrude","SWEPT_FACE",FACE,{"disambiguationData":[OSD([subQ0])]}),"instanceName":"3"})})])],"derivedFrom":makeQuery(id+"F16.opBoolean","MERGE",FACE,{"derivedFrom":[makeQuery(id+"F14.opBoolean","COPY",FACE,{"derivedFrom":makeQuery(id+"F13.opPattern","COPY",FACE,{"derivedFrom":subQ3,"instanceName":"1"})}),makeQuery(id+"F14.opBoolean","COPY",FACE,{"derivedFrom":makeQuery(id+"F13.opPattern","COPY",FACE,{"derivedFrom":subQ3,"instanceName":"3"})}),makeQuery(id+"F14.opBoolean","COPY",FACE,{"derivedFrom":makeQuery(id+"F13.opPattern","COPY",FACE,{"derivedFrom":subQ3,"instanceName":"5"})}),makeQuery(id+"F14.opBoolean","COPY",FACE,{"derivedFrom":makeQuery(id+"F13.opPattern","COPY",FACE,{"derivedFrom":subQ3,"instanceName":"7"})}),makeQuery(id+"F14.opBoolean","COPY",FACE,{"derivedFrom":makeQuery(id+"F13.opPattern","COPY",FACE,{"derivedFrom":subQ3,"instanceName":"9"})})],"fromTools":[makeQuery(id+"F15.opPattern","COPY",FACE,{"derivedFrom":subQ3,"instanceName":"1"}),makeQuery(id+"F15.opPattern","COPY",FACE,{"derivedFrom":makeQuery(id+"F13.opPattern","COPY",FACE,{"derivedFrom":subQ3,"instanceName":"2"}),"instanceName":"1"}),makeQuery(id+"F15.opPattern","COPY",FACE,{"derivedFrom":makeQuery(id+"F13.opPattern","COPY",FACE,{"derivedFrom":subQ3,"instanceName":"4"}),"instanceName":"1"}),makeQuery(id+"F15.opPattern","COPY",FACE,{"derivedFrom":makeQuery(id+"F13.opPattern","COPY",FACE,{"derivedFrom":subQ3,"instanceName":"6"}),"instanceName":"1"}),makeQuery(id+"F15.opPattern","COPY",FACE,{"derivedFrom":makeQuery(id+"F13.opPattern","COPY",FACE,{"derivedFrom":subQ3,"instanceName":"8"}),"instanceName":"1"})]})})]});}
            var Q18;
            {var subQ0=sQuery(id+"F11.wireOp",EDGE,"E18.filletArc");var subQ2=sQuery(id+"F11.wireOp",EDGE,"E11");var subQ4=makeQuery(id+"F12.opExtrude","SWEPT_FACE",FACE,{"disambiguationData":[OSD([subQ2])]});var subQ5=sQuery(id+"F18.wireOp",EDGE,"E28");Q18=makeQuery(id+"F25.opBoolean","INTERSECT",EDGE,{"derivedFrom":[makeQuery(id+"F23.opPattern","COPY",FACE,{"derivedFrom":makeQuery(id+"F21.opBoolean","MERGE",FACE,{"derivedFrom":[makeQuery(id+"F19.opExtrude","SWEPT_FACE",FACE,{"disambiguationData":[OSD([subQ5])]}),makeQuery(id+"F20.opExtrude","SWEPT_FACE",FACE,{"disambiguationData":[OSD([subQ5])]})]}),"instanceName":"5"}),makeQuery(id+"F24.opBoolean","SPLIT",FACE,{"disambiguationData":[TD([makeQuery(id+"F14.opBoolean","COPY",FACE,{"derivedFrom":makeQuery(id+"F13.opPattern","COPY",FACE,{"derivedFrom":makeQuery(id+"F12.opExtrude","SWEPT_FACE",FACE,{"disambiguationData":[OSD([subQ0])]}),"instanceName":"3"})})])],"derivedFrom":makeQuery(id+"F16.opBoolean","MERGE",FACE,{"derivedFrom":[makeQuery(id+"F14.opBoolean","COPY",FACE,{"derivedFrom":makeQuery(id+"F13.opPattern","COPY",FACE,{"derivedFrom":subQ4,"instanceName":"1"})}),makeQuery(id+"F14.opBoolean","COPY",FACE,{"derivedFrom":makeQuery(id+"F13.opPattern","COPY",FACE,{"derivedFrom":subQ4,"instanceName":"3"})}),makeQuery(id+"F14.opBoolean","COPY",FACE,{"derivedFrom":makeQuery(id+"F13.opPattern","COPY",FACE,{"derivedFrom":subQ4,"instanceName":"5"})}),makeQuery(id+"F14.opBoolean","COPY",FACE,{"derivedFrom":makeQuery(id+"F13.opPattern","COPY",FACE,{"derivedFrom":subQ4,"instanceName":"7"})}),makeQuery(id+"F14.opBoolean","COPY",FACE,{"derivedFrom":makeQuery(id+"F13.opPattern","COPY",FACE,{"derivedFrom":subQ4,"instanceName":"9"})})],"fromTools":[makeQuery(id+"F15.opPattern","COPY",FACE,{"derivedFrom":subQ4,"instanceName":"1"}),makeQuery(id+"F15.opPattern","COPY",FACE,{"derivedFrom":makeQuery(id+"F13.opPattern","COPY",FACE,{"derivedFrom":subQ4,"instanceName":"2"}),"instanceName":"1"}),makeQuery(id+"F15.opPattern","COPY",FACE,{"derivedFrom":makeQuery(id+"F13.opPattern","COPY",FACE,{"derivedFrom":subQ4,"instanceName":"4"}),"instanceName":"1"}),makeQuery(id+"F15.opPattern","COPY",FACE,{"derivedFrom":makeQuery(id+"F13.opPattern","COPY",FACE,{"derivedFrom":subQ4,"instanceName":"6"}),"instanceName":"1"}),makeQuery(id+"F15.opPattern","COPY",FACE,{"derivedFrom":makeQuery(id+"F13.opPattern","COPY",FACE,{"derivedFrom":subQ4,"instanceName":"8"}),"instanceName":"1"})]})})]});}
            var Q19;
            {var subQ0=sQuery(id+"F11.wireOp",EDGE,"E18.filletArc");var subQ1=sQuery(id+"F11.wireOp",EDGE,"E11");var subQ3=makeQuery(id+"F12.opExtrude","SWEPT_FACE",FACE,{"disambiguationData":[OSD([subQ1])]});var subQ4=sQuery(id+"F18.wireOp",EDGE,"E28");Q19=makeQuery(id+"F25.opBoolean","INTERSECT",EDGE,{"derivedFrom":[makeQuery(id+"F23.opPattern","COPY",FACE,{"derivedFrom":makeQuery(id+"F21.opBoolean","MERGE",FACE,{"derivedFrom":[makeQuery(id+"F19.opExtrude","SWEPT_FACE",FACE,{"disambiguationData":[OSD([subQ4])]}),makeQuery(id+"F20.opExtrude","SWEPT_FACE",FACE,{"disambiguationData":[OSD([subQ4])]})]}),"instanceName":"7"}),makeQuery(id+"F24.opBoolean","SPLIT",FACE,{"disambiguationData":[TD([makeQuery(id+"F14.opBoolean","COPY",FACE,{"derivedFrom":makeQuery(id+"F13.opPattern","COPY",FACE,{"derivedFrom":makeQuery(id+"F12.opExtrude","SWEPT_FACE",FACE,{"disambiguationData":[OSD([subQ0])]}),"instanceName":"5"})})])],"derivedFrom":makeQuery(id+"F16.opBoolean","MERGE",FACE,{"derivedFrom":[makeQuery(id+"F14.opBoolean","COPY",FACE,{"derivedFrom":makeQuery(id+"F13.opPattern","COPY",FACE,{"derivedFrom":subQ3,"instanceName":"1"})}),makeQuery(id+"F14.opBoolean","COPY",FACE,{"derivedFrom":makeQuery(id+"F13.opPattern","COPY",FACE,{"derivedFrom":subQ3,"instanceName":"3"})}),makeQuery(id+"F14.opBoolean","COPY",FACE,{"derivedFrom":makeQuery(id+"F13.opPattern","COPY",FACE,{"derivedFrom":subQ3,"instanceName":"5"})}),makeQuery(id+"F14.opBoolean","COPY",FACE,{"derivedFrom":makeQuery(id+"F13.opPattern","COPY",FACE,{"derivedFrom":subQ3,"instanceName":"7"})}),makeQuery(id+"F14.opBoolean","COPY",FACE,{"derivedFrom":makeQuery(id+"F13.opPattern","COPY",FACE,{"derivedFrom":subQ3,"instanceName":"9"})})],"fromTools":[makeQuery(id+"F15.opPattern","COPY",FACE,{"derivedFrom":subQ3,"instanceName":"1"}),makeQuery(id+"F15.opPattern","COPY",FACE,{"derivedFrom":makeQuery(id+"F13.opPattern","COPY",FACE,{"derivedFrom":subQ3,"instanceName":"2"}),"instanceName":"1"}),makeQuery(id+"F15.opPattern","COPY",FACE,{"derivedFrom":makeQuery(id+"F13.opPattern","COPY",FACE,{"derivedFrom":subQ3,"instanceName":"4"}),"instanceName":"1"}),makeQuery(id+"F15.opPattern","COPY",FACE,{"derivedFrom":makeQuery(id+"F13.opPattern","COPY",FACE,{"derivedFrom":subQ3,"instanceName":"6"}),"instanceName":"1"}),makeQuery(id+"F15.opPattern","COPY",FACE,{"derivedFrom":makeQuery(id+"F13.opPattern","COPY",FACE,{"derivedFrom":subQ3,"instanceName":"8"}),"instanceName":"1"})]})})]});}
            var Q20;
            {var subQ0=sQuery(id+"F11.wireOp",EDGE,"E18.filletArc");var subQ1=sQuery(id+"F11.wireOp",EDGE,"E11");var subQ3=makeQuery(id+"F12.opExtrude","SWEPT_FACE",FACE,{"disambiguationData":[OSD([subQ1])]});var subQ4=sQuery(id+"F18.wireOp",EDGE,"E28");Q20=makeQuery(id+"F25.opBoolean","INTERSECT",EDGE,{"derivedFrom":[makeQuery(id+"F23.opPattern","COPY",FACE,{"derivedFrom":makeQuery(id+"F21.opBoolean","MERGE",FACE,{"derivedFrom":[makeQuery(id+"F19.opExtrude","SWEPT_FACE",FACE,{"disambiguationData":[OSD([subQ4])]}),makeQuery(id+"F20.opExtrude","SWEPT_FACE",FACE,{"disambiguationData":[OSD([subQ4])]})]}),"instanceName":"9"}),makeQuery(id+"F24.opBoolean","SPLIT",FACE,{"disambiguationData":[TD([makeQuery(id+"F14.opBoolean","COPY",FACE,{"derivedFrom":makeQuery(id+"F13.opPattern","COPY",FACE,{"derivedFrom":makeQuery(id+"F12.opExtrude","SWEPT_FACE",FACE,{"disambiguationData":[OSD([subQ0])]}),"instanceName":"7"})})])],"derivedFrom":makeQuery(id+"F16.opBoolean","MERGE",FACE,{"derivedFrom":[makeQuery(id+"F14.opBoolean","COPY",FACE,{"derivedFrom":makeQuery(id+"F13.opPattern","COPY",FACE,{"derivedFrom":subQ3,"instanceName":"1"})}),makeQuery(id+"F14.opBoolean","COPY",FACE,{"derivedFrom":makeQuery(id+"F13.opPattern","COPY",FACE,{"derivedFrom":subQ3,"instanceName":"3"})}),makeQuery(id+"F14.opBoolean","COPY",FACE,{"derivedFrom":makeQuery(id+"F13.opPattern","COPY",FACE,{"derivedFrom":subQ3,"instanceName":"5"})}),makeQuery(id+"F14.opBoolean","COPY",FACE,{"derivedFrom":makeQuery(id+"F13.opPattern","COPY",FACE,{"derivedFrom":subQ3,"instanceName":"7"})}),makeQuery(id+"F14.opBoolean","COPY",FACE,{"derivedFrom":makeQuery(id+"F13.opPattern","COPY",FACE,{"derivedFrom":subQ3,"instanceName":"9"})})],"fromTools":[makeQuery(id+"F15.opPattern","COPY",FACE,{"derivedFrom":subQ3,"instanceName":"1"}),makeQuery(id+"F15.opPattern","COPY",FACE,{"derivedFrom":makeQuery(id+"F13.opPattern","COPY",FACE,{"derivedFrom":subQ3,"instanceName":"2"}),"instanceName":"1"}),makeQuery(id+"F15.opPattern","COPY",FACE,{"derivedFrom":makeQuery(id+"F13.opPattern","COPY",FACE,{"derivedFrom":subQ3,"instanceName":"4"}),"instanceName":"1"}),makeQuery(id+"F15.opPattern","COPY",FACE,{"derivedFrom":makeQuery(id+"F13.opPattern","COPY",FACE,{"derivedFrom":subQ3,"instanceName":"6"}),"instanceName":"1"}),makeQuery(id+"F15.opPattern","COPY",FACE,{"derivedFrom":makeQuery(id+"F13.opPattern","COPY",FACE,{"derivedFrom":subQ3,"instanceName":"8"}),"instanceName":"1"})]})})]});}
            var Q21;
            {var subQ0=sQuery(id+"F11.wireOp",EDGE,"E19.filletArc");var subQ2=sQuery(id+"F11.wireOp",EDGE,"E11");var subQ5=makeQuery(id+"F12.opExtrude","SWEPT_FACE",FACE,{"disambiguationData":[OSD([subQ2])]});var subQ6=sQuery(id+"F18.wireOp",EDGE,"E28");Q21=makeQuery(id+"F25.opBoolean","INTERSECT",EDGE,{"derivedFrom":[makeQuery(id+"F23.opPattern","COPY",FACE,{"derivedFrom":makeQuery(id+"F21.opBoolean","MERGE",FACE,{"derivedFrom":[makeQuery(id+"F19.opExtrude","SWEPT_FACE",FACE,{"disambiguationData":[OSD([subQ6])]}),makeQuery(id+"F20.opExtrude","SWEPT_FACE",FACE,{"disambiguationData":[OSD([subQ6])]})]}),"instanceName":"9"}),makeQuery(id+"F24.opBoolean","SPLIT",FACE,{"disambiguationData":[TD([makeQuery(id+"F14.opBoolean","COPY",FACE,{"derivedFrom":makeQuery(id+"F13.opPattern","COPY",FACE,{"derivedFrom":makeQuery(id+"F12.opExtrude","SWEPT_FACE",FACE,{"disambiguationData":[OSD([subQ0])]}),"instanceName":"9"})})])],"derivedFrom":makeQuery(id+"F16.opBoolean","MERGE",FACE,{"derivedFrom":[makeQuery(id+"F14.opBoolean","COPY",FACE,{"derivedFrom":makeQuery(id+"F13.opPattern","COPY",FACE,{"derivedFrom":subQ5,"instanceName":"1"})}),makeQuery(id+"F14.opBoolean","COPY",FACE,{"derivedFrom":makeQuery(id+"F13.opPattern","COPY",FACE,{"derivedFrom":subQ5,"instanceName":"3"})}),makeQuery(id+"F14.opBoolean","COPY",FACE,{"derivedFrom":makeQuery(id+"F13.opPattern","COPY",FACE,{"derivedFrom":subQ5,"instanceName":"5"})}),makeQuery(id+"F14.opBoolean","COPY",FACE,{"derivedFrom":makeQuery(id+"F13.opPattern","COPY",FACE,{"derivedFrom":subQ5,"instanceName":"7"})}),makeQuery(id+"F14.opBoolean","COPY",FACE,{"derivedFrom":makeQuery(id+"F13.opPattern","COPY",FACE,{"derivedFrom":subQ5,"instanceName":"9"})})],"fromTools":[makeQuery(id+"F15.opPattern","COPY",FACE,{"derivedFrom":subQ5,"instanceName":"1"}),makeQuery(id+"F15.opPattern","COPY",FACE,{"derivedFrom":makeQuery(id+"F13.opPattern","COPY",FACE,{"derivedFrom":subQ5,"instanceName":"2"}),"instanceName":"1"}),makeQuery(id+"F15.opPattern","COPY",FACE,{"derivedFrom":makeQuery(id+"F13.opPattern","COPY",FACE,{"derivedFrom":subQ5,"instanceName":"4"}),"instanceName":"1"}),makeQuery(id+"F15.opPattern","COPY",FACE,{"derivedFrom":makeQuery(id+"F13.opPattern","COPY",FACE,{"derivedFrom":subQ5,"instanceName":"6"}),"instanceName":"1"}),makeQuery(id+"F15.opPattern","COPY",FACE,{"derivedFrom":makeQuery(id+"F13.opPattern","COPY",FACE,{"derivedFrom":subQ5,"instanceName":"8"}),"instanceName":"1"})]})})]});}
            var Q22;
            {var subQ0=sQuery(id+"F11.wireOp",EDGE,"E18.filletArc");var subQ2=sQuery(id+"F11.wireOp",EDGE,"E11");var subQ5=makeQuery(id+"F12.opExtrude","SWEPT_FACE",FACE,{"disambiguationData":[OSD([subQ2])]});var subQ6=sQuery(id+"F18.wireOp",EDGE,"E28");Q22=makeQuery(id+"F25.opBoolean","INTERSECT",EDGE,{"derivedFrom":[makeQuery(id+"F21.opBoolean","MERGE",FACE,{"derivedFrom":[makeQuery(id+"F19.opExtrude","SWEPT_FACE",FACE,{"disambiguationData":[OSD([subQ6])]}),makeQuery(id+"F20.opExtrude","SWEPT_FACE",FACE,{"disambiguationData":[OSD([subQ6])]})]}),makeQuery(id+"F24.opBoolean","SPLIT",FACE,{"disambiguationData":[TD([makeQuery(id+"F14.opBoolean","COPY",FACE,{"derivedFrom":makeQuery(id+"F13.opPattern","COPY",FACE,{"derivedFrom":makeQuery(id+"F12.opExtrude","SWEPT_FACE",FACE,{"disambiguationData":[OSD([subQ0])]}),"instanceName":"9"})})])],"derivedFrom":makeQuery(id+"F16.opBoolean","MERGE",FACE,{"derivedFrom":[makeQuery(id+"F14.opBoolean","COPY",FACE,{"derivedFrom":makeQuery(id+"F13.opPattern","COPY",FACE,{"derivedFrom":subQ5,"instanceName":"1"})}),makeQuery(id+"F14.opBoolean","COPY",FACE,{"derivedFrom":makeQuery(id+"F13.opPattern","COPY",FACE,{"derivedFrom":subQ5,"instanceName":"3"})}),makeQuery(id+"F14.opBoolean","COPY",FACE,{"derivedFrom":makeQuery(id+"F13.opPattern","COPY",FACE,{"derivedFrom":subQ5,"instanceName":"5"})}),makeQuery(id+"F14.opBoolean","COPY",FACE,{"derivedFrom":makeQuery(id+"F13.opPattern","COPY",FACE,{"derivedFrom":subQ5,"instanceName":"7"})}),makeQuery(id+"F14.opBoolean","COPY",FACE,{"derivedFrom":makeQuery(id+"F13.opPattern","COPY",FACE,{"derivedFrom":subQ5,"instanceName":"9"})})],"fromTools":[makeQuery(id+"F15.opPattern","COPY",FACE,{"derivedFrom":subQ5,"instanceName":"1"}),makeQuery(id+"F15.opPattern","COPY",FACE,{"derivedFrom":makeQuery(id+"F13.opPattern","COPY",FACE,{"derivedFrom":subQ5,"instanceName":"2"}),"instanceName":"1"}),makeQuery(id+"F15.opPattern","COPY",FACE,{"derivedFrom":makeQuery(id+"F13.opPattern","COPY",FACE,{"derivedFrom":subQ5,"instanceName":"4"}),"instanceName":"1"}),makeQuery(id+"F15.opPattern","COPY",FACE,{"derivedFrom":makeQuery(id+"F13.opPattern","COPY",FACE,{"derivedFrom":subQ5,"instanceName":"6"}),"instanceName":"1"}),makeQuery(id+"F15.opPattern","COPY",FACE,{"derivedFrom":makeQuery(id+"F13.opPattern","COPY",FACE,{"derivedFrom":subQ5,"instanceName":"8"}),"instanceName":"1"})]})})]});}
            var Q23;
            {var subQ0=sQuery(id+"F11.wireOp",EDGE,"E13");var subQ1=sQuery(id+"F11.wireOp",EDGE,"E18.filletArc");var subQ2=sQuery(id+"F18.wireOp",EDGE,"E28");Q23=makeQuery(id+"F25.opBoolean","INTERSECT",EDGE,{"derivedFrom":[makeQuery(id+"F21.opBoolean","MERGE",FACE,{"derivedFrom":[makeQuery(id+"F19.opExtrude","SWEPT_FACE",FACE,{"disambiguationData":[OSD([subQ2])]}),makeQuery(id+"F20.opExtrude","SWEPT_FACE",FACE,{"disambiguationData":[OSD([subQ2])]})]}),makeQuery(id+"F24.opBoolean","SPLIT",FACE,{"disambiguationData":[TD([makeQuery(id+"F14.opBoolean","COPY",FACE,{"derivedFrom":makeQuery(id+"F13.opPattern","COPY",FACE,{"derivedFrom":makeQuery(id+"F12.opExtrude","SWEPT_FACE",FACE,{"disambiguationData":[OSD([subQ0])]}),"instanceName":"9"})})])],"derivedFrom":makeQuery(id+"F14.opBoolean","COPY",FACE,{"derivedFrom":makeQuery(id+"F13.opPattern","COPY",FACE,{"derivedFrom":makeQuery(id+"F12.opExtrude","SWEPT_FACE",FACE,{"disambiguationData":[OSD([subQ1])]}),"instanceName":"9"})})})]});}
            fillet(context, id + "F26", {"entities" : qUnion([Q0, Q1, Q2, Q3, Q4, Q5, Q6, Q7, Q8, Q9, Q10, Q11, Q12, Q13, Q14, Q15, Q16, Q17, Q18, Q19, Q20, Q21, Q22, Q23]), "radius" : 2 * mm, "tangentPropagation" : true, "allowEdgeOverflow" : false});
        }
        {
            var Q0;
            Q0=makeQuery(id+"F2.imprint","IMPRINT",FACE,{"disambiguationData":[TD([[makeQuery(id+"F2.imprint","IMPRINT",EDGE,{"derivedFrom":sQuery(id+"F2.wireOp",EDGE,"E1")}),-1.0]])]});
            var sketch = newSketch(context, id + "F27", { "sketchPlane" : qUnion([Q0])});
            skArc(sketch, "E32.0", {"start": v(-13.02, -8.85) * mm, "mid": v(-13.01, -9.02) * mm, "end": v(-13.03, -9.2) * mm});
            skArc(sketch, "E33.0", {"start": v(-12.76, -10.41) * mm, "mid": v(-13, -9.83) * mm, "end": v(-13.03, -9.2) * mm});
            skArc(sketch, "E34.0", {"start": v(-12.76, -10.41) * mm, "mid": v(-11.66, -10.91) * mm, "end": v(-10.48, -10.68) * mm});
            skLineSegment(sketch, "E35.0", {"start": v(-10.48, -10.68) * mm, "end": v(-10.07, -10.47) * mm});
            skArc(sketch, "E36.0", {"start": v(-8.78, -10.45) * mm, "mid": v(-9.8, -11.9) * mm, "end": v(-9.27, -13.6) * mm});
            skArc(sketch, "E37.0", {"start": v(-8.14, -13.71) * mm, "mid": v(-8.7, -13.74) * mm, "end": v(-9.27, -13.6) * mm});
            skArc(sketch, "E38.0", {"start": v(-8.14, -13.71) * mm, "mid": v(-7.76, -13.68) * mm, "end": v(-7.38, -13.72) * mm});
            skLineSegment(sketch, "E39.0", {"start": v(-7.94, -10) * mm, "end": v(-8.78, -10.45) * mm});
            skLineSegment(sketch, "E40.0", {"start": v(-13.4, 6.66) * mm, "end": v(-12.67, 5.97) * mm});
            skArc(sketch, "E41.0", {"start": v(-14.01, 7.93) * mm, "mid": v(-13.82, 7.24) * mm, "end": v(-13.4, 6.66) * mm});
            skArc(sketch, "E42.0", {"start": v(-12.85, 8.67) * mm, "mid": v(-13.27, 8.28) * mm, "end": v(-13.78, 8.03) * mm});
            skArc(sketch, "E43.0", {"start": v(9.07, -13.21) * mm, "mid": v(9.4, -12.44) * mm, "end": v(10.01, -11.86) * mm});
            skArc(sketch, "E44.0", {"start": v(7.22, -11.58) * mm, "mid": v(7.86, -12.71) * mm, "end": v(9.07, -13.21) * mm});
            skLineSegment(sketch, "E45.0", {"start": v(7.03, -10.5) * mm, "end": v(7.22, -11.58) * mm});
            skArc(sketch, "E46", {"start": v(-12.85, 8.67) * mm, "mid": v(-13.29, 7.29) * mm, "end": v(-12.67, 5.97) * mm});
            skArc(sketch, "E47", {"start": v(-13.02, -8.85) * mm, "mid": v(-11.99, -10.46) * mm, "end": v(-10.07, -10.47) * mm});
            skArc(sketch, "E48", {"start": v(-7.94, -10) * mm, "mid": v(-8.97, -12.05) * mm, "end": v(-7.38, -13.72) * mm});
            skArc(sketch, "E49", {"start": v(7.03, -10.5) * mm, "mid": v(8.17, -11.96) * mm, "end": v(10.01, -11.86) * mm});
            skPoint(sketch, "E50.orphan", {"position": v(-14.26, -7.14) * mm});
            skPoint(sketch, "E51.orphan", {"position": v(-7.34, -8.99) * mm});
            skPoint(sketch, "E52.orphan", {"position": v(-5.99, -14.78) * mm});
            skPoint(sketch, "E53.orphan", {"position": v(-10.82, 4.2) * mm});
            skPoint(sketch, "E54.orphan", {"position": v(-12.42, 10) * mm});
            skPoint(sketch, "E55.orphan", {"position": v(6.46, -7.43) * mm});
            skPoint(sketch, "E56.orphan", {"position": v(10.96, -11.58) * mm});
            skArc(sketch, "E57.0", {"start": v(-14.01, 7.93) * mm, "mid": v(-13.9, 7.98) * mm, "end": v(-13.78, 8.03) * mm});
            skArc(sketch, "E58", {"start": v(12.79, 3.35) * mm, "mid": v(14.18, 3.69) * mm, "end": v(15, 4.87) * mm});
            skArc(sketch, "E59.0", {"start": v(13.24, 3.3) * mm, "mid": v(14.2, 3.4) * mm, "end": v(15, 3.94) * mm});
            skArc(sketch, "E60.0", {"start": v(15, 3.94) * mm, "mid": v(14.94, 4.4) * mm, "end": v(15, 4.87) * mm});
            skLineSegment(sketch, "E61.0", {"start": v(12.79, 3.35) * mm, "end": v(13.24, 3.3) * mm});
            skPoint(sketch, "E62.orphan", {"position": v(15.09, 5.15) * mm});
            skPoint(sketch, "E63.orphan", {"position": v(9.06, 3.85) * mm});
            skSolve(sketch);
        }
        {
            var Q0;
            {Q0=qUnion([makeQuery(id+"F27.imprint","IMPRINT",FACE,{"disambiguationData":[TD([[makeQuery(id+"F27.imprint","IMPRINT",EDGE,{"derivedFrom":sQuery(id+"F27.wireOp",EDGE,"E32.0")}),1.0]])]}),makeQuery(id+"F27.imprint","IMPRINT",FACE,{"disambiguationData":[TD([[makeQuery(id+"F27.imprint","IMPRINT",EDGE,{"derivedFrom":sQuery(id+"F27.wireOp",EDGE,"E36.0")}),1.0]])]}),makeQuery(id+"F27.imprint","IMPRINT",FACE,{"disambiguationData":[TD([[makeQuery(id+"F27.imprint","IMPRINT",EDGE,{"derivedFrom":sQuery(id+"F27.wireOp",EDGE,"E40.0")}),1.0]])]}),makeQuery(id+"F27.imprint","IMPRINT",FACE,{"disambiguationData":[TD([[makeQuery(id+"F27.imprint","IMPRINT",EDGE,{"derivedFrom":sQuery(id+"F27.wireOp",EDGE,"E43.0")}),1.0]])]}),makeQuery(id+"F27.imprint","IMPRINT",FACE,{"disambiguationData":[TD([[makeQuery(id+"F27.imprint","IMPRINT",EDGE,{"derivedFrom":sQuery(id+"F27.wireOp",EDGE,"E58")}),-1.0]])]})]);}
            var Q1;
            Q1=makeQuery(id+"F14.opBoolean","COPY",FACE,{"derivedFrom":makeQuery(id+"F13.opPattern","COPY",FACE,{"derivedFrom":makeQuery(id+"F12.opExtrude","CAP_FACE",FACE,{"disambiguationData":[OSD([sQuery(id+"F11.wireOp",EDGE,"E11"),sQuery(id+"F11.wireOp",EDGE,"E12"),sQuery(id+"F11.wireOp",EDGE,"E13"),sQuery(id+"F11.wireOp",EDGE,"E14"),sQuery(id+"F11.wireOp",EDGE,"E17.filletArc"),sQuery(id+"F11.wireOp",EDGE,"E18.filletArc"),sQuery(id+"F11.wireOp",EDGE,"E19.filletArc"),sQuery(id+"F11.wireOp",EDGE,"E20.filletArc")])],"isStart":true}),"instanceName":"1"})});
            extrude(context, id + "F28", {"entities" : qUnion([Q0]), "operationType" : NewBodyOperationType.ADD, "endBound" : BoundingType.UP_TO_SURFACE, "oppositeDirection" : true, "endBoundEntityFace" : qUnion([Q1]), "depth" : 25 * mm});
        }
        {
            var Q0;
            {var subQ0=makeQuery(id+"F20.opExtrude","CAP_FACE",FACE,{"disambiguationData":[OSD([sQuery(id+"F18.wireOp",EDGE,"E27"),sQuery(id+"F18.wireOp",EDGE,"E28"),sQuery(id+"F18.wireOp",EDGE,"E29"),sQuery(id+"F18.wireOp",EDGE,"E30.trimOffspring")])],"isStart":false});Q0=makeQuery(id+"F25.opBoolean","MERGE",FACE,{"derivedFrom":[subQ0,makeQuery(id+"F23.opPattern","COPY",FACE,{"derivedFrom":subQ0,"instanceName":"1"}),makeQuery(id+"F23.opPattern","COPY",FACE,{"derivedFrom":subQ0,"instanceName":"2"}),makeQuery(id+"F23.opPattern","COPY",FACE,{"derivedFrom":subQ0,"instanceName":"3"}),makeQuery(id+"F23.opPattern","COPY",FACE,{"derivedFrom":subQ0,"instanceName":"4"}),makeQuery(id+"F23.opPattern","COPY",FACE,{"derivedFrom":subQ0,"instanceName":"5"}),makeQuery(id+"F23.opPattern","COPY",FACE,{"derivedFrom":subQ0,"instanceName":"6"}),makeQuery(id+"F23.opPattern","COPY",FACE,{"derivedFrom":subQ0,"instanceName":"7"}),makeQuery(id+"F23.opPattern","COPY",FACE,{"derivedFrom":subQ0,"instanceName":"8"}),makeQuery(id+"F23.opPattern","COPY",FACE,{"derivedFrom":subQ0,"instanceName":"9"}),makeQuery(id+"F23.opPattern","COPY",FACE,{"derivedFrom":subQ0,"instanceName":"10"}),makeQuery(id+"F1.opRevolve","SWEPT_FACE",FACE,{"disambiguationData":[OSD([sQuery(id+"F0.wireOp",EDGE,"E0.left")])]})]});}
            var sketch = newSketch(context, id + "F29", { "sketchPlane" : qUnion([Q0])});
            skArc(sketch, "E64.0", {"start": v(-15.02, -4.27) * mm, "mid": v(-14.7, -4.9) * mm, "end": v(-14.63, -5.58) * mm});
            skArc(sketch, "E65.0", {"start": v(-12.65, -5.12) * mm, "mid": v(-13.58, -5.62) * mm, "end": v(-14.63, -5.58) * mm});
            skLineSegment(sketch, "E66.0", {"start": v(-12.03, -4.53) * mm, "end": v(-12.65, -5.12) * mm});
            skArc(sketch, "E67.0", {"start": v(-0.02, -16.3) * mm, "mid": v(-0.31, -16.14) * mm, "end": v(-0.57, -15.94) * mm});
            skArc(sketch, "E68.0", {"start": v(-1.64, -15.41) * mm, "mid": v(-1.07, -15.6) * mm, "end": v(-0.57, -15.94) * mm});
            skArc(sketch, "E69.0", {"start": v(0.96, -13.61) * mm, "mid": v(1.04, -15.16) * mm, "end": v(-0.02, -16.3) * mm});
            skLineSegment(sketch, "E70.0", {"start": v(0.46, -12.57) * mm, "end": v(0.96, -13.61) * mm});
            skArc(sketch, "E71.0", {"start": v(16.29, -1.38) * mm, "mid": v(15.66, -2.12) * mm, "end": v(14.76, -2.48) * mm});
            skArc(sketch, "E72.0", {"start": v(15.93, -0.7) * mm, "mid": v(16.14, -1.02) * mm, "end": v(16.29, -1.38) * mm});
            skArc(sketch, "E73.0", {"start": v(15.93, -0.7) * mm, "mid": v(15.72, -0.38) * mm, "end": v(15.58, -0.03) * mm});
            skLineSegment(sketch, "E74.0", {"start": v(14.76, -2.48) * mm, "end": v(13.93, -2.6) * mm});
            skArc(sketch, "E75", {"start": v(-15.02, -4.27) * mm, "mid": v(-13.58, -5.08) * mm, "end": v(-12.03, -4.53) * mm});
            skArc(sketch, "E76", {"start": v(-1.64, -15.41) * mm, "mid": v(0.27, -14.63) * mm, "end": v(0.46, -12.57) * mm});
            skArc(sketch, "E77", {"start": v(13.93, -2.6) * mm, "mid": v(15.35, -1.7) * mm, "end": v(15.58, -0.03) * mm});
            skPoint(sketch, "E78.orphan", {"position": v(15.85, 1.7) * mm});
            skPoint(sketch, "E79.orphan", {"position": v(11.22, -2.96) * mm});
            skPoint(sketch, "E80.orphan", {"position": v(-0.86, -9.8) * mm});
            skPoint(sketch, "E81.orphan", {"position": v(-2.95, -15.67) * mm});
            skPoint(sketch, "E82.orphan", {"position": v(-9.6, -2.21) * mm});
            skPoint(sketch, "E83.orphan", {"position": v(-15.48, -3.82) * mm});
            skSolve(sketch);
        }
        {
            var Q0;
            {Q0=qUnion([makeQuery(id+"F29.imprint","IMPRINT",FACE,{"disambiguationData":[TD([[makeQuery(id+"F29.imprint","IMPRINT",EDGE,{"derivedFrom":sQuery(id+"F29.wireOp",EDGE,"E64.0")}),1.0]])]}),makeQuery(id+"F29.imprint","IMPRINT",FACE,{"disambiguationData":[TD([[makeQuery(id+"F29.imprint","IMPRINT",EDGE,{"derivedFrom":sQuery(id+"F29.wireOp",EDGE,"E67.0")}),-1.0]])]}),makeQuery(id+"F29.imprint","IMPRINT",FACE,{"disambiguationData":[TD([[makeQuery(id+"F29.imprint","IMPRINT",EDGE,{"derivedFrom":sQuery(id+"F29.wireOp",EDGE,"E71.0")}),-1.0]])]})]);}
            var Q1;
            Q1=makeQuery(id+"F28.boolean.opBoolean","MERGE",FACE,{"derivedFrom":[makeQuery(id+"F16.opBoolean","COPY",FACE,{"derivedFrom":makeQuery(id+"F15.opPattern","COPY",FACE,{"derivedFrom":makeQuery(id+"F13.opPattern","COPY",FACE,{"derivedFrom":makeQuery(id+"F12.opExtrude","CAP_FACE",FACE,{"disambiguationData":[OSD([sQuery(id+"F11.wireOp",EDGE,"E11"),sQuery(id+"F11.wireOp",EDGE,"E12"),sQuery(id+"F11.wireOp",EDGE,"E13"),sQuery(id+"F11.wireOp",EDGE,"E14"),sQuery(id+"F11.wireOp",EDGE,"E17.filletArc"),sQuery(id+"F11.wireOp",EDGE,"E18.filletArc"),sQuery(id+"F11.wireOp",EDGE,"E19.filletArc"),sQuery(id+"F11.wireOp",EDGE,"E20.filletArc")])],"isStart":true}),"instanceName":"6"}),"instanceName":"1"})}),makeQuery(id+"F28.opExtrude","CAP_FACE",FACE,{"disambiguationData":[OSD([sQuery(id+"F27.wireOp",EDGE,"E43.0"),sQuery(id+"F27.wireOp",EDGE,"E44.0"),sQuery(id+"F27.wireOp",EDGE,"E45.0"),sQuery(id+"F27.wireOp",EDGE,"E49")])],"isStart":false})]});
            extrude(context, id + "F30", {"entities" : qUnion([Q0]), "operationType" : NewBodyOperationType.ADD, "endBound" : BoundingType.UP_TO_SURFACE, "oppositeDirection" : true, "endBoundEntityFace" : qUnion([Q1]), "depth" : 25 * mm});
        }
        {
            var Q0;
            Q0=qCreatedBy(makeId("Front.planeOp"),FACE);
            var sketch = newSketch(context, id + "F31", { "sketchPlane" : qUnion([Q0])});
            skLineSegment(sketch, "E84", {"start": v(0, 0) * mm, "end": v(0, 22) * mm, "construction": true});
            skLineSegment(sketch, "E85", {"start": v(-2.5, 9) * mm, "end": v(-1, 16.5) * mm});
            skLineSegment(sketch, "E86", {"start": v(-1, 16.5) * mm, "end": v(-1, 19) * mm});
            skLineSegment(sketch, "E87", {"start": v(-1, 19) * mm, "end": v(-0.5, 22) * mm});
            skLineSegment(sketch, "E88", {"start": v(-0.5, 22) * mm, "end": v(0, 22) * mm});
            skLineSegment(sketch, "E89", {"start": v(-2.5, 9) * mm, "end": v(-2.5, 0) * mm});
            skLineSegment(sketch, "E90", {"start": v(0, 0) * mm, "end": v(-2.5, 0) * mm});
            skLineSegment(sketch, "E91.0.MirrorCS", {"start": v(1, 19) * mm, "end": v(0.5, 22) * mm});
            skLineSegment(sketch, "E91.1.MirrorCS", {"start": v(0, 0) * mm, "end": v(2.5, 0) * mm});
            skLineSegment(sketch, "E91.2.MirrorCS", {"start": v(2.5, 9) * mm, "end": v(2.5, 0) * mm});
            skLineSegment(sketch, "E91.3.MirrorCS", {"start": v(1, 16.5) * mm, "end": v(1, 19) * mm});
            skLineSegment(sketch, "E91.4.MirrorCS", {"start": v(2.5, 9) * mm, "end": v(1, 16.5) * mm});
            skLineSegment(sketch, "E91.5.MirrorCS", {"start": v(0.5, 22) * mm, "end": v(0, 22) * mm});
            skSolve(sketch);
        }
        {
            var Q0;
            Q0 = qSketchRegion(id + "F31", true);
            var Q1;
            Q1=sQuery(id+"F31.wireOp",EDGE,"E91.1.MirrorCS");
            revolve(context, id + "F32", {"entities" : qUnion([Q0]), "axis" : qUnion([Q1]), "revolveType" : RevolveType.FULL});
        }
        {
            var Q0;
            Q0=makeQuery(id+"F32.opRevolve","SWEPT_EDGE",EDGE,{"disambiguationData":[OSD([sQuery(id+"F31.wireOp",EDGE,"E85"),sQuery(id+"F31.wireOp",EDGE,"E86")])]});
            var Q1;
            Q1=makeQuery(id+"F32.opRevolve","SWEPT_EDGE",EDGE,{"disambiguationData":[OSD([sQuery(id+"F31.wireOp",EDGE,"E86"),sQuery(id+"F31.wireOp",EDGE,"E87")])]});
            var Q2;
            Q2=makeQuery(id+"F32.opRevolve","SWEPT_EDGE",EDGE,{"disambiguationData":[OSD([sQuery(id+"F31.wireOp",EDGE,"E91.3.MirrorCS"),sQuery(id+"F31.wireOp",EDGE,"E91.4.MirrorCS")])]});
            var Q3;
            Q3=makeQuery(id+"F32.opRevolve","SWEPT_EDGE",EDGE,{"disambiguationData":[OSD([sQuery(id+"F31.wireOp",EDGE,"E91.0.MirrorCS"),sQuery(id+"F31.wireOp",EDGE,"E91.3.MirrorCS")])]});
            fillet(context, id + "F33", {"entities" : qUnion([Q0, Q1, Q2, Q3]), "radius" : 10 * mm, "tangentPropagation" : true, "allowEdgeOverflow" : false});
        }
        {
            var Q0;
            Q0=makeQuery(id+"F32.opRevolve","SWEPT_EDGE",EDGE,{"disambiguationData":[OSD([sQuery(id+"F31.wireOp",EDGE,"E91.0.MirrorCS"),sQuery(id+"F31.wireOp",EDGE,"E91.5.MirrorCS")])]});
            var Q1;
            Q1=makeQuery(id+"F32.opRevolve","SWEPT_EDGE",EDGE,{"disambiguationData":[OSD([sQuery(id+"F31.wireOp",EDGE,"E87"),sQuery(id+"F31.wireOp",EDGE,"E91.5.MirrorCS")])]});
            fillet(context, id + "F34", {"entities" : qUnion([Q0, Q1]), "radius" : .3 * mm, "tangentPropagation" : true, "allowEdgeOverflow" : false});
        }
        {
            var Q0;
            Q0=makeQuery(id+"F23.opPattern","COPY",BODY,{"derivedFrom":makeQuery(id+"F19.opExtrude","SWEPT_BODY",BODY,{"disambiguationData":[OSD([sQuery(id+"F18.wireOp",EDGE,"E27"),sQuery(id+"F18.wireOp",EDGE,"E28"),sQuery(id+"F18.wireOp",EDGE,"E29"),sQuery(id+"F18.wireOp",EDGE,"E30.trimOffspring")])]}),"instanceName":"1"});
            var Q1;
            Q1=makeQuery(id+"F32.opRevolve","SWEPT_BODY",BODY,{"disambiguationData":[OSD([sQuery(id+"F31.wireOp",EDGE,"E85"),sQuery(id+"F31.wireOp",EDGE,"E86"),sQuery(id+"F31.wireOp",EDGE,"E87"),sQuery(id+"F31.wireOp",EDGE,"E89"),sQuery(id+"F31.wireOp",EDGE,"E90"),sQuery(id+"F31.wireOp",EDGE,"E91.0.MirrorCS"),sQuery(id+"F31.wireOp",EDGE,"E91.2.MirrorCS"),sQuery(id+"F31.wireOp",EDGE,"E91.3.MirrorCS"),sQuery(id+"F31.wireOp",EDGE,"E91.4.MirrorCS"),sQuery(id+"F31.wireOp",EDGE,"E91.5.MirrorCS")])]});
            booleanBodies(context, id + "F35", {"operationType" : BooleanOperationType.INTERSECTION, "tools" : qUnion([Q0, Q1])});
        }
        {
            var Q0;
            Q0=makeQuery(id+"F24.opBoolean","COPY",FACE,{"derivedFrom":makeQuery(id+"F23.opPattern","COPY",FACE,{"derivedFrom":makeQuery(id+"F22.opExtrude","SWEPT_FACE",FACE,{"disambiguationData":[OSD([sQuery(id+"F18.wireOp",EDGE,"E21")])]}),"instanceName":"9"})});
            var Q1;
            Q1=makeQuery(id+"F24.opBoolean","COPY",FACE,{"derivedFrom":makeQuery(id+"F23.opPattern","COPY",FACE,{"derivedFrom":makeQuery(id+"F22.opExtrude","SWEPT_FACE",FACE,{"disambiguationData":[OSD([sQuery(id+"F18.wireOp",EDGE,"E21")])]}),"instanceName":"8"})});
            var Q2;
            Q2=makeQuery(id+"F24.opBoolean","COPY",FACE,{"derivedFrom":makeQuery(id+"F23.opPattern","COPY",FACE,{"derivedFrom":makeQuery(id+"F22.opExtrude","SWEPT_FACE",FACE,{"disambiguationData":[OSD([sQuery(id+"F18.wireOp",EDGE,"E21")])]}),"instanceName":"7"})});
            var Q3;
            Q3=makeQuery(id+"F24.opBoolean","COPY",FACE,{"derivedFrom":makeQuery(id+"F23.opPattern","COPY",FACE,{"derivedFrom":makeQuery(id+"F22.opExtrude","SWEPT_FACE",FACE,{"disambiguationData":[OSD([sQuery(id+"F18.wireOp",EDGE,"E21")])]}),"instanceName":"6"})});
            var Q4;
            Q4=makeQuery(id+"F24.opBoolean","COPY",FACE,{"derivedFrom":makeQuery(id+"F23.opPattern","COPY",FACE,{"derivedFrom":makeQuery(id+"F22.opExtrude","SWEPT_FACE",FACE,{"disambiguationData":[OSD([sQuery(id+"F18.wireOp",EDGE,"E21")])]}),"instanceName":"5"})});
            var Q5;
            Q5=makeQuery(id+"F24.opBoolean","COPY",FACE,{"derivedFrom":makeQuery(id+"F23.opPattern","COPY",FACE,{"derivedFrom":makeQuery(id+"F22.opExtrude","SWEPT_FACE",FACE,{"disambiguationData":[OSD([sQuery(id+"F18.wireOp",EDGE,"E21")])]}),"instanceName":"4"})});
            var Q6;
            Q6=makeQuery(id+"F24.opBoolean","COPY",FACE,{"derivedFrom":makeQuery(id+"F23.opPattern","COPY",FACE,{"derivedFrom":makeQuery(id+"F22.opExtrude","SWEPT_FACE",FACE,{"disambiguationData":[OSD([sQuery(id+"F18.wireOp",EDGE,"E21")])]}),"instanceName":"3"})});
            var Q7;
            Q7=makeQuery(id+"F24.opBoolean","COPY",FACE,{"derivedFrom":makeQuery(id+"F23.opPattern","COPY",FACE,{"derivedFrom":makeQuery(id+"F22.opExtrude","SWEPT_FACE",FACE,{"disambiguationData":[OSD([sQuery(id+"F18.wireOp",EDGE,"E21")])]}),"instanceName":"2"})});
            var Q8;
            Q8=makeQuery(id+"F24.opBoolean","COPY",FACE,{"derivedFrom":makeQuery(id+"F23.opPattern","COPY",FACE,{"derivedFrom":makeQuery(id+"F22.opExtrude","SWEPT_FACE",FACE,{"disambiguationData":[OSD([sQuery(id+"F18.wireOp",EDGE,"E21")])]}),"instanceName":"1"})});
            var Q9;
            Q9=makeQuery(id+"F24.opBoolean","COPY",FACE,{"derivedFrom":makeQuery(id+"F22.opExtrude","SWEPT_FACE",FACE,{"disambiguationData":[OSD([sQuery(id+"F18.wireOp",EDGE,"E21")])]})});
            var Q10;
            Q10=makeQuery(id+"F24.opBoolean","COPY",FACE,{"derivedFrom":makeQuery(id+"F23.opPattern","COPY",FACE,{"derivedFrom":makeQuery(id+"F22.opExtrude","SWEPT_FACE",FACE,{"disambiguationData":[OSD([sQuery(id+"F18.wireOp",EDGE,"E21")])]}),"instanceName":"10"})});
            fillet(context, id + "F36", {"entities" : qUnion([Q0, Q1, Q2, Q3, Q4, Q5, Q6, Q7, Q8, Q9, Q10]), "radius" : .2 * mm, "tangentPropagation" : true, "allowEdgeOverflow" : false});
        }
        {
            var Q0;
            {var subQ0=sQuery(id+"F18.wireOp",EDGE,"E27");Q0=makeQuery(id+"F25.opBoolean","MERGE",FACE,{"derivedFrom":[makeQuery(id+"F23.opPattern","COPY",FACE,{"derivedFrom":makeQuery(id+"F21.opBoolean","MERGE",FACE,{"derivedFrom":[makeQuery(id+"F19.opExtrude","SWEPT_FACE",FACE,{"disambiguationData":[OSD([subQ0])]}),makeQuery(id+"F20.opExtrude","SWEPT_FACE",FACE,{"disambiguationData":[OSD([subQ0])]})]}),"instanceName":"10"}),makeQuery(id+"F24.opBoolean","COPY",FACE,{"derivedFrom":makeQuery(id+"F23.opPattern","COPY",FACE,{"derivedFrom":makeQuery(id+"F22.opExtrude","SWEPT_FACE",FACE,{"disambiguationData":[OSD([subQ0])]}),"instanceName":"10"})})]});}
            var Q1;
            {var subQ0=sQuery(id+"F18.wireOp",EDGE,"E27");Q1=makeQuery(id+"F25.opBoolean","MERGE",FACE,{"derivedFrom":[makeQuery(id+"F21.opBoolean","MERGE",FACE,{"derivedFrom":[makeQuery(id+"F19.opExtrude","SWEPT_FACE",FACE,{"disambiguationData":[OSD([subQ0])]}),makeQuery(id+"F20.opExtrude","SWEPT_FACE",FACE,{"disambiguationData":[OSD([subQ0])]})]}),makeQuery(id+"F24.opBoolean","COPY",FACE,{"derivedFrom":makeQuery(id+"F22.opExtrude","SWEPT_FACE",FACE,{"disambiguationData":[OSD([subQ0])]})})]});}
            var Q2;
            {var subQ0=sQuery(id+"F18.wireOp",EDGE,"E27");Q2=makeQuery(id+"F25.opBoolean","MERGE",FACE,{"derivedFrom":[makeQuery(id+"F23.opPattern","COPY",FACE,{"derivedFrom":makeQuery(id+"F21.opBoolean","MERGE",FACE,{"derivedFrom":[makeQuery(id+"F19.opExtrude","SWEPT_FACE",FACE,{"disambiguationData":[OSD([subQ0])]}),makeQuery(id+"F20.opExtrude","SWEPT_FACE",FACE,{"disambiguationData":[OSD([subQ0])]})]}),"instanceName":"1"}),makeQuery(id+"F24.opBoolean","COPY",FACE,{"derivedFrom":makeQuery(id+"F23.opPattern","COPY",FACE,{"derivedFrom":makeQuery(id+"F22.opExtrude","SWEPT_FACE",FACE,{"disambiguationData":[OSD([subQ0])]}),"instanceName":"1"})})]});}
            var Q3;
            {var subQ0=sQuery(id+"F18.wireOp",EDGE,"E27");Q3=makeQuery(id+"F25.opBoolean","MERGE",FACE,{"derivedFrom":[makeQuery(id+"F23.opPattern","COPY",FACE,{"derivedFrom":makeQuery(id+"F21.opBoolean","MERGE",FACE,{"derivedFrom":[makeQuery(id+"F19.opExtrude","SWEPT_FACE",FACE,{"disambiguationData":[OSD([subQ0])]}),makeQuery(id+"F20.opExtrude","SWEPT_FACE",FACE,{"disambiguationData":[OSD([subQ0])]})]}),"instanceName":"2"}),makeQuery(id+"F24.opBoolean","COPY",FACE,{"derivedFrom":makeQuery(id+"F23.opPattern","COPY",FACE,{"derivedFrom":makeQuery(id+"F22.opExtrude","SWEPT_FACE",FACE,{"disambiguationData":[OSD([subQ0])]}),"instanceName":"2"})})]});}
            var Q4;
            {var subQ0=sQuery(id+"F18.wireOp",EDGE,"E27");Q4=makeQuery(id+"F25.opBoolean","MERGE",FACE,{"derivedFrom":[makeQuery(id+"F23.opPattern","COPY",FACE,{"derivedFrom":makeQuery(id+"F21.opBoolean","MERGE",FACE,{"derivedFrom":[makeQuery(id+"F19.opExtrude","SWEPT_FACE",FACE,{"disambiguationData":[OSD([subQ0])]}),makeQuery(id+"F20.opExtrude","SWEPT_FACE",FACE,{"disambiguationData":[OSD([subQ0])]})]}),"instanceName":"3"}),makeQuery(id+"F24.opBoolean","COPY",FACE,{"derivedFrom":makeQuery(id+"F23.opPattern","COPY",FACE,{"derivedFrom":makeQuery(id+"F22.opExtrude","SWEPT_FACE",FACE,{"disambiguationData":[OSD([subQ0])]}),"instanceName":"3"})})]});}
            var Q5;
            {var subQ0=sQuery(id+"F18.wireOp",EDGE,"E27");Q5=makeQuery(id+"F25.opBoolean","MERGE",FACE,{"derivedFrom":[makeQuery(id+"F23.opPattern","COPY",FACE,{"derivedFrom":makeQuery(id+"F21.opBoolean","MERGE",FACE,{"derivedFrom":[makeQuery(id+"F19.opExtrude","SWEPT_FACE",FACE,{"disambiguationData":[OSD([subQ0])]}),makeQuery(id+"F20.opExtrude","SWEPT_FACE",FACE,{"disambiguationData":[OSD([subQ0])]})]}),"instanceName":"9"}),makeQuery(id+"F24.opBoolean","COPY",FACE,{"derivedFrom":makeQuery(id+"F23.opPattern","COPY",FACE,{"derivedFrom":makeQuery(id+"F22.opExtrude","SWEPT_FACE",FACE,{"disambiguationData":[OSD([subQ0])]}),"instanceName":"9"})})]});}
            var Q6;
            {var subQ0=sQuery(id+"F18.wireOp",EDGE,"E27");Q6=makeQuery(id+"F25.opBoolean","MERGE",FACE,{"derivedFrom":[makeQuery(id+"F23.opPattern","COPY",FACE,{"derivedFrom":makeQuery(id+"F21.opBoolean","MERGE",FACE,{"derivedFrom":[makeQuery(id+"F19.opExtrude","SWEPT_FACE",FACE,{"disambiguationData":[OSD([subQ0])]}),makeQuery(id+"F20.opExtrude","SWEPT_FACE",FACE,{"disambiguationData":[OSD([subQ0])]})]}),"instanceName":"8"}),makeQuery(id+"F24.opBoolean","COPY",FACE,{"derivedFrom":makeQuery(id+"F23.opPattern","COPY",FACE,{"derivedFrom":makeQuery(id+"F22.opExtrude","SWEPT_FACE",FACE,{"disambiguationData":[OSD([subQ0])]}),"instanceName":"8"})})]});}
            var Q7;
            {var subQ0=sQuery(id+"F18.wireOp",EDGE,"E27");Q7=makeQuery(id+"F25.opBoolean","MERGE",FACE,{"derivedFrom":[makeQuery(id+"F23.opPattern","COPY",FACE,{"derivedFrom":makeQuery(id+"F21.opBoolean","MERGE",FACE,{"derivedFrom":[makeQuery(id+"F19.opExtrude","SWEPT_FACE",FACE,{"disambiguationData":[OSD([subQ0])]}),makeQuery(id+"F20.opExtrude","SWEPT_FACE",FACE,{"disambiguationData":[OSD([subQ0])]})]}),"instanceName":"7"}),makeQuery(id+"F24.opBoolean","COPY",FACE,{"derivedFrom":makeQuery(id+"F23.opPattern","COPY",FACE,{"derivedFrom":makeQuery(id+"F22.opExtrude","SWEPT_FACE",FACE,{"disambiguationData":[OSD([subQ0])]}),"instanceName":"7"})})]});}
            var Q8;
            {var subQ0=sQuery(id+"F18.wireOp",EDGE,"E27");Q8=makeQuery(id+"F25.opBoolean","MERGE",FACE,{"derivedFrom":[makeQuery(id+"F23.opPattern","COPY",FACE,{"derivedFrom":makeQuery(id+"F21.opBoolean","MERGE",FACE,{"derivedFrom":[makeQuery(id+"F19.opExtrude","SWEPT_FACE",FACE,{"disambiguationData":[OSD([subQ0])]}),makeQuery(id+"F20.opExtrude","SWEPT_FACE",FACE,{"disambiguationData":[OSD([subQ0])]})]}),"instanceName":"6"}),makeQuery(id+"F24.opBoolean","COPY",FACE,{"derivedFrom":makeQuery(id+"F23.opPattern","COPY",FACE,{"derivedFrom":makeQuery(id+"F22.opExtrude","SWEPT_FACE",FACE,{"disambiguationData":[OSD([subQ0])]}),"instanceName":"6"})})]});}
            var Q9;
            {var subQ0=sQuery(id+"F18.wireOp",EDGE,"E27");Q9=makeQuery(id+"F25.opBoolean","MERGE",FACE,{"derivedFrom":[makeQuery(id+"F23.opPattern","COPY",FACE,{"derivedFrom":makeQuery(id+"F21.opBoolean","MERGE",FACE,{"derivedFrom":[makeQuery(id+"F19.opExtrude","SWEPT_FACE",FACE,{"disambiguationData":[OSD([subQ0])]}),makeQuery(id+"F20.opExtrude","SWEPT_FACE",FACE,{"disambiguationData":[OSD([subQ0])]})]}),"instanceName":"4"}),makeQuery(id+"F24.opBoolean","COPY",FACE,{"derivedFrom":makeQuery(id+"F23.opPattern","COPY",FACE,{"derivedFrom":makeQuery(id+"F22.opExtrude","SWEPT_FACE",FACE,{"disambiguationData":[OSD([subQ0])]}),"instanceName":"4"})})]});}
            var Q10;
            {var subQ0=sQuery(id+"F18.wireOp",EDGE,"E27");Q10=makeQuery(id+"F25.opBoolean","MERGE",FACE,{"derivedFrom":[makeQuery(id+"F23.opPattern","COPY",FACE,{"derivedFrom":makeQuery(id+"F21.opBoolean","MERGE",FACE,{"derivedFrom":[makeQuery(id+"F19.opExtrude","SWEPT_FACE",FACE,{"disambiguationData":[OSD([subQ0])]}),makeQuery(id+"F20.opExtrude","SWEPT_FACE",FACE,{"disambiguationData":[OSD([subQ0])]})]}),"instanceName":"5"}),makeQuery(id+"F24.opBoolean","COPY",FACE,{"derivedFrom":makeQuery(id+"F23.opPattern","COPY",FACE,{"derivedFrom":makeQuery(id+"F22.opExtrude","SWEPT_FACE",FACE,{"disambiguationData":[OSD([subQ0])]}),"instanceName":"5"})})]});}
            chamfer(context, id + "F37", {"entities" : qUnion([Q0, Q1, Q2, Q3, Q4, Q5, Q6, Q7, Q8, Q9, Q10]), "width" : .1 * mm, "tangentPropagation" : true});
        }
    });
